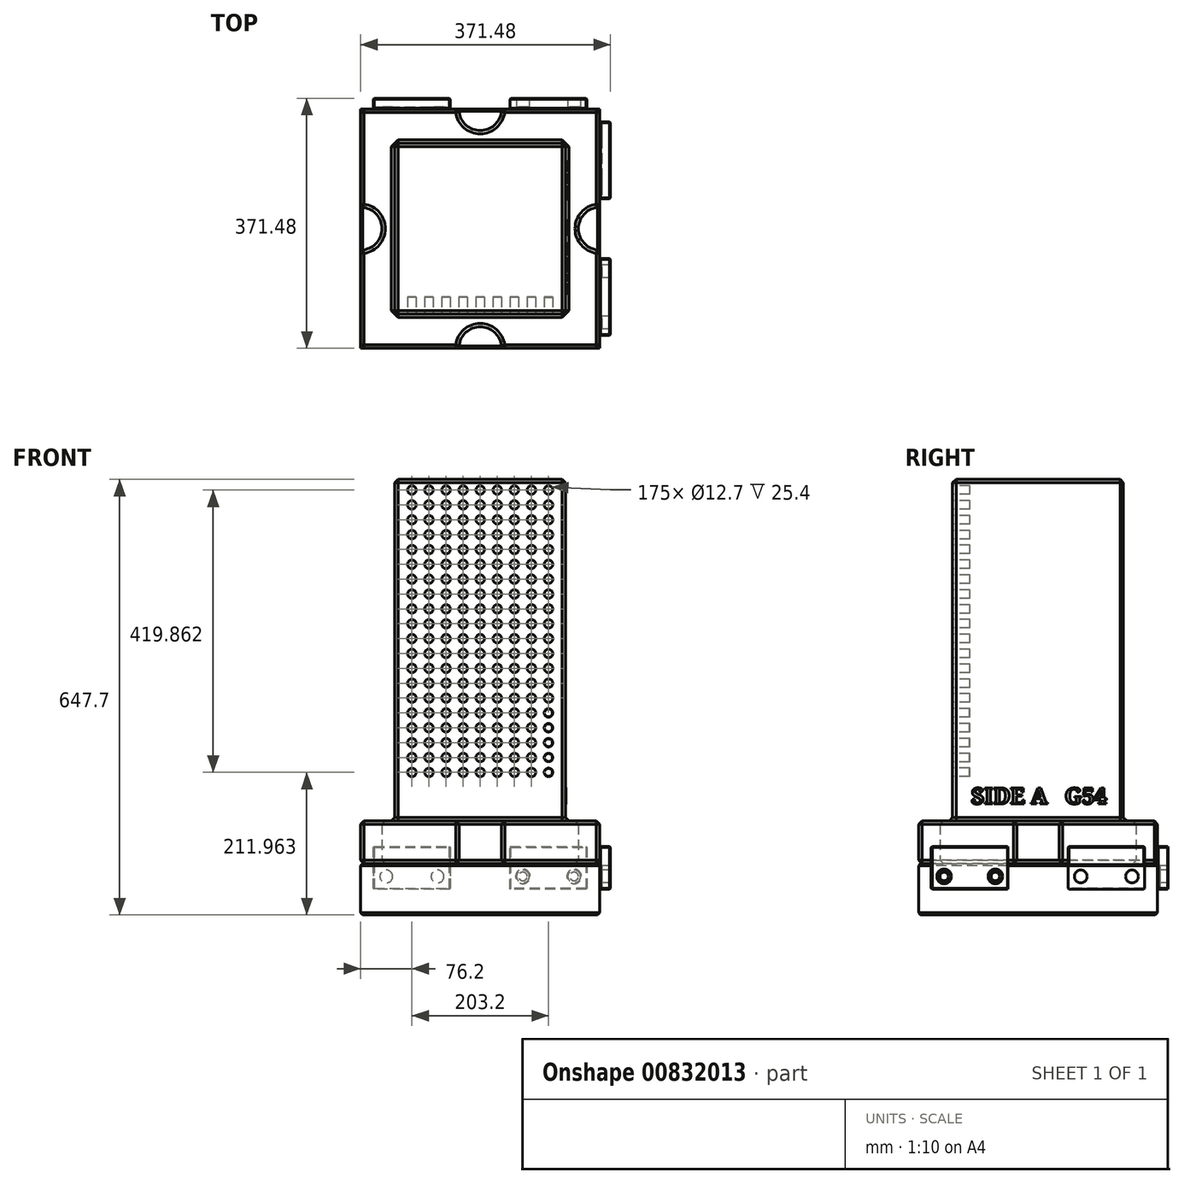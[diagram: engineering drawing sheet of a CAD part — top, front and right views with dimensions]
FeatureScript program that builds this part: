
annotation { "Feature Type Name" : "Feature", "Feature Type Description" : "" }
export const myFeature = defineFeature(function(context is Context, id is Id, definition is map)
    precondition{}
    {
        {
            var Q0;
            Q0=qCreatedBy(makeId("Top.planeOp"),FACE);
            var sketch = newSketch(context, id + "F0", { "sketchPlane" : qUnion([Q0])});
            skLineSegment(sketch, "E0.bottom", {"start": v(-127, -127) * mm, "end": v(127, -127) * mm});
            skLineSegment(sketch, "E0.top", {"start": v(-127, 127) * mm, "end": v(127, 127) * mm});
            skLineSegment(sketch, "E0.left", {"start": v(-127, -127) * mm, "end": v(-127, 127) * mm});
            skLineSegment(sketch, "E0.right", {"start": v(127, -127) * mm, "end": v(127, 127) * mm});
            skPoint(sketch, "E0.middle", {"position": v(0, 0) * mm});
            skLineSegment(sketch, "E1.bottom", {"start": v(-177.8, -177.8) * mm, "end": v(177.8, -177.8) * mm});
            skLineSegment(sketch, "E1.top", {"start": v(-177.8, 177.8) * mm, "end": v(177.8, 177.8) * mm});
            skLineSegment(sketch, "E1.left", {"start": v(-177.8, -177.8) * mm, "end": v(-177.8, 177.8) * mm});
            skLineSegment(sketch, "E1.right", {"start": v(177.8, -177.8) * mm, "end": v(177.8, 177.8) * mm});
            skSolve(sketch);
        }
        {
            var Q0;
            Q0=makeQuery(id+"F0.imprint","IMPRINT",FACE,{"disambiguationData":[TD([[makeQuery(id+"F0.imprint","IMPRINT",EDGE,{"derivedFrom":sQuery(id+"F0.wireOp",EDGE,"E0.bottom")}),1.0]])]});
            extrude(context, id + "F1", {"entities" : qUnion([Q0]), "depth" : 508 * mm});
        }
        {
            var Q0;
            Q0=makeQuery(id+"F0.imprint","IMPRINT",FACE,{"disambiguationData":[TD([[makeQuery(id+"F0.imprint","IMPRINT",EDGE,{"derivedFrom":sQuery(id+"F0.wireOp",EDGE,"E0.bottom")}),-1.0]])]});
            var Q1;
            Q1=makeQuery(id+"F0.imprint","IMPRINT",FACE,{"disambiguationData":[TD([[makeQuery(id+"F0.imprint","IMPRINT",EDGE,{"derivedFrom":sQuery(id+"F0.wireOp",EDGE,"E0.bottom")}),1.0]])]});
            extrude(context, id + "F2", {"entities" : qUnion([Q0, Q1]), "operationType" : NewBodyOperationType.ADD, "oppositeDirection" : true, "depth" : 63.5 * mm});
        }
        {
            var Q0;
            Q0=makeQuery(id+"F2.opExtrude","CAP_FACE",FACE,{"disambiguationData":[OSD([sQuery(id+"F0.wireOp",EDGE,"E1.bottom"),sQuery(id+"F0.wireOp",EDGE,"E1.top"),sQuery(id+"F0.wireOp",EDGE,"E1.left"),sQuery(id+"F0.wireOp",EDGE,"E1.right")])],"isStart":false});
            var sketch = newSketch(context, id + "F3", { "sketchPlane" : qUnion([Q0])});
            skCircle(sketch, "E2", {"center": v(-177.8, 0) * mm, "radius": 31.75 * mm});
            skCircle(sketch, "E3", {"center": v(177.8, 0) * mm, "radius": 31.75 * mm});
            skCircle(sketch, "E4", {"center": v(0, -177.8) * mm, "radius": 31.75 * mm});
            skCircle(sketch, "E5", {"center": v(0, 177.8) * mm, "radius": 31.75 * mm});
            skSolve(sketch);
        }
        {
            var Q0;
            {var subQ0=sQuery(id+"F3.wireOp",EDGE,"E5");var subQ1=makeQuery(id+"F2.opExtrude","CAP_EDGE",EDGE,{"disambiguationData":[OSD([sQuery(id+"F0.wireOp",EDGE,"E1.bottom")])],"isStart":false});var subQ2=makeQuery(id+"F3.imprint","INTERSECT",VERTEX,{"disambiguationData":[OD(0.0)],"derivedFrom":[subQ1,subQ0]});Q0=makeQuery(id+"F3.imprint","IMPRINT",FACE,{"disambiguationData":[TD([[makeQuery(id+"F3.imprint","IMPRINT",EDGE,{"disambiguationData":[TD([[subQ2,-1.0]])],"derivedFrom":subQ0}),1.0]])]});}
            var Q1;
            {var subQ0=sQuery(id+"F3.wireOp",EDGE,"E3");var subQ1=makeQuery(id+"F2.opExtrude","CAP_EDGE",EDGE,{"disambiguationData":[OSD([sQuery(id+"F0.wireOp",EDGE,"E1.right")])],"isStart":false});var subQ2=makeQuery(id+"F3.imprint","INTERSECT",VERTEX,{"disambiguationData":[OD(0.0)],"derivedFrom":[subQ1,subQ0]});Q1=makeQuery(id+"F3.imprint","IMPRINT",FACE,{"disambiguationData":[TD([[makeQuery(id+"F3.imprint","IMPRINT",EDGE,{"disambiguationData":[TD([[subQ2,-1.0]])],"derivedFrom":subQ0}),1.0]])]});}
            var Q2;
            {var subQ0=sQuery(id+"F3.wireOp",EDGE,"E2");var subQ1=makeQuery(id+"F2.opExtrude","CAP_EDGE",EDGE,{"disambiguationData":[OSD([sQuery(id+"F0.wireOp",EDGE,"E1.left")])],"isStart":false});var subQ2=makeQuery(id+"F3.imprint","INTERSECT",VERTEX,{"disambiguationData":[OD(0.0)],"derivedFrom":[subQ1,subQ0]});Q2=makeQuery(id+"F3.imprint","IMPRINT",FACE,{"disambiguationData":[TD([[makeQuery(id+"F3.imprint","IMPRINT",EDGE,{"disambiguationData":[TD([[subQ2,1.0]])],"derivedFrom":subQ0}),1.0]])]});}
            var Q3;
            {var subQ0=sQuery(id+"F3.wireOp",EDGE,"E4");var subQ1=makeQuery(id+"F2.opExtrude","CAP_EDGE",EDGE,{"disambiguationData":[OSD([sQuery(id+"F0.wireOp",EDGE,"E1.top")])],"isStart":false});var subQ2=makeQuery(id+"F3.imprint","INTERSECT",VERTEX,{"disambiguationData":[OD(0.0)],"derivedFrom":[subQ1,subQ0]});Q3=makeQuery(id+"F3.imprint","IMPRINT",FACE,{"disambiguationData":[TD([[makeQuery(id+"F3.imprint","IMPRINT",EDGE,{"disambiguationData":[TD([[subQ2,1.0]])],"derivedFrom":subQ0}),1.0]])]});}
            var Q4;
            Q4=makeQuery(id+"F2.opExtrude","CAP_FACE",FACE,{"disambiguationData":[OSD([sQuery(id+"F0.wireOp",EDGE,"E1.bottom"),sQuery(id+"F0.wireOp",EDGE,"E1.top"),sQuery(id+"F0.wireOp",EDGE,"E1.left"),sQuery(id+"F0.wireOp",EDGE,"E1.right")])],"isStart":true});
            extrude(context, id + "F4", {"entities" : qUnion([Q0, Q1, Q2, Q3]), "operationType" : NewBodyOperationType.REMOVE, "endBound" : BoundingType.UP_TO_SURFACE, "oppositeDirection" : true, "endBoundEntityFace" : qUnion([Q4]), "depth" : 25.4 * mm});
        }
        {
            var Q0;
            Q0=makeQuery(id+"F1.opExtrude","CAP_FACE",FACE,{"disambiguationData":[OSD([sQuery(id+"F0.wireOp",EDGE,"E0.bottom"),sQuery(id+"F0.wireOp",EDGE,"E0.top"),sQuery(id+"F0.wireOp",EDGE,"E0.left"),sQuery(id+"F0.wireOp",EDGE,"E0.right")])],"isStart":false});
            var Q1;
            Q1=makeQuery(id+"F1.opExtrude","SWEPT_FACE",FACE,{"disambiguationData":[OSD([sQuery(id+"F0.wireOp",EDGE,"E0.right")])]});
            var Q2;
            Q2=makeQuery(id+"F1.opExtrude","SWEPT_FACE",FACE,{"disambiguationData":[OSD([sQuery(id+"F0.wireOp",EDGE,"E0.top")])]});
            var Q3;
            Q3=makeQuery(id+"F1.opExtrude","SWEPT_FACE",FACE,{"disambiguationData":[OSD([sQuery(id+"F0.wireOp",EDGE,"E0.left")])]});
            var Q4;
            Q4=makeQuery(id+"F1.opExtrude","SWEPT_FACE",FACE,{"disambiguationData":[OSD([sQuery(id+"F0.wireOp",EDGE,"E0.bottom")])]});
            var Q5;
            {var subQ1=sQuery(id+"F0.wireOp",EDGE,"E1.left");var subQ3=sQuery(id+"F0.wireOp",EDGE,"E1.bottom");Q5=makeQuery(id+"F4.boolean.opBoolean","SPLIT",FACE,{"disambiguationData":[TD([makeQuery(id+"F2.opExtrude","SWEPT_FACE",FACE,{"disambiguationData":[OSD([subQ1])]})])],"derivedFrom":makeQuery(id+"F2.opExtrude","SWEPT_FACE",FACE,{"disambiguationData":[OSD([subQ3])]})});}
            var Q6;
            {var subQ0=sQuery(id+"F0.wireOp",EDGE,"E1.right");var subQ3=sQuery(id+"F0.wireOp",EDGE,"E1.bottom");Q6=makeQuery(id+"F4.boolean.opBoolean","SPLIT",FACE,{"disambiguationData":[TD([makeQuery(id+"F2.opExtrude","SWEPT_FACE",FACE,{"disambiguationData":[OSD([subQ0])]})])],"derivedFrom":makeQuery(id+"F2.opExtrude","SWEPT_FACE",FACE,{"disambiguationData":[OSD([subQ3])]})});}
            var Q7;
            Q7=makeQuery(id+"F4.boolean.opBoolean","COPY",FACE,{"derivedFrom":makeQuery(id+"F4.opExtrude","SWEPT_FACE",FACE,{"disambiguationData":[OSD([sQuery(id+"F3.wireOp",EDGE,"E5")])]})});
            var Q8;
            Q8=makeQuery(id+"F4.boolean.opBoolean","COPY",FACE,{"derivedFrom":makeQuery(id+"F4.opExtrude","SWEPT_FACE",FACE,{"disambiguationData":[OSD([sQuery(id+"F3.wireOp",EDGE,"E3")])]})});
            var Q9;
            {var subQ0=sQuery(id+"F0.wireOp",EDGE,"E1.bottom");var subQ1=sQuery(id+"F0.wireOp",EDGE,"E1.right");Q9=makeQuery(id+"F4.boolean.opBoolean","SPLIT",FACE,{"disambiguationData":[TD([makeQuery(id+"F2.opExtrude","SWEPT_FACE",FACE,{"disambiguationData":[OSD([subQ0])]})])],"derivedFrom":makeQuery(id+"F2.opExtrude","SWEPT_FACE",FACE,{"disambiguationData":[OSD([subQ1])]})});}
            var Q10;
            {var subQ0=sQuery(id+"F0.wireOp",EDGE,"E1.right");var subQ2=sQuery(id+"F0.wireOp",EDGE,"E1.top");Q10=makeQuery(id+"F4.boolean.opBoolean","SPLIT",FACE,{"disambiguationData":[TD([makeQuery(id+"F2.opExtrude","SWEPT_FACE",FACE,{"disambiguationData":[OSD([subQ2])]})])],"derivedFrom":makeQuery(id+"F2.opExtrude","SWEPT_FACE",FACE,{"disambiguationData":[OSD([subQ0])]})});}
            var Q11;
            {var subQ0=sQuery(id+"F0.wireOp",EDGE,"E1.right");var subQ2=sQuery(id+"F0.wireOp",EDGE,"E1.top");Q11=makeQuery(id+"F4.boolean.opBoolean","SPLIT",FACE,{"disambiguationData":[TD([makeQuery(id+"F2.opExtrude","SWEPT_FACE",FACE,{"disambiguationData":[OSD([subQ0])]})])],"derivedFrom":makeQuery(id+"F2.opExtrude","SWEPT_FACE",FACE,{"disambiguationData":[OSD([subQ2])]})});}
            var Q12;
            Q12=makeQuery(id+"F4.boolean.opBoolean","COPY",FACE,{"derivedFrom":makeQuery(id+"F4.opExtrude","SWEPT_FACE",FACE,{"disambiguationData":[OSD([sQuery(id+"F3.wireOp",EDGE,"E4")])]})});
            var Q13;
            {var subQ1=sQuery(id+"F0.wireOp",EDGE,"E1.left");var subQ2=sQuery(id+"F0.wireOp",EDGE,"E1.top");Q13=makeQuery(id+"F4.boolean.opBoolean","SPLIT",FACE,{"disambiguationData":[TD([makeQuery(id+"F2.opExtrude","SWEPT_FACE",FACE,{"disambiguationData":[OSD([subQ1])]})])],"derivedFrom":makeQuery(id+"F2.opExtrude","SWEPT_FACE",FACE,{"disambiguationData":[OSD([subQ2])]})});}
            var Q14;
            {var subQ1=sQuery(id+"F0.wireOp",EDGE,"E1.left");var subQ2=sQuery(id+"F0.wireOp",EDGE,"E1.top");Q14=makeQuery(id+"F4.boolean.opBoolean","SPLIT",FACE,{"disambiguationData":[TD([makeQuery(id+"F2.opExtrude","SWEPT_FACE",FACE,{"disambiguationData":[OSD([subQ2])]})])],"derivedFrom":makeQuery(id+"F2.opExtrude","SWEPT_FACE",FACE,{"disambiguationData":[OSD([subQ1])]})});}
            var Q15;
            Q15=makeQuery(id+"F4.boolean.opBoolean","COPY",FACE,{"derivedFrom":makeQuery(id+"F4.opExtrude","SWEPT_FACE",FACE,{"disambiguationData":[OSD([sQuery(id+"F3.wireOp",EDGE,"E2")])]})});
            var Q16;
            {var subQ0=sQuery(id+"F0.wireOp",EDGE,"E1.bottom");var subQ2=sQuery(id+"F0.wireOp",EDGE,"E1.left");Q16=makeQuery(id+"F4.boolean.opBoolean","SPLIT",FACE,{"disambiguationData":[TD([makeQuery(id+"F2.opExtrude","SWEPT_FACE",FACE,{"disambiguationData":[OSD([subQ0])]})])],"derivedFrom":makeQuery(id+"F2.opExtrude","SWEPT_FACE",FACE,{"disambiguationData":[OSD([subQ2])]})});}
            chamfer(context, id + "F5", {"entities" : qUnion([Q0, Q1, Q2, Q3, Q4, Q5, Q6, Q7, Q8, Q9, Q10, Q11, Q12, Q13, Q14, Q15, Q16]), "width" : 5.08 * mm, "tangentPropagation" : true});
        }
        {
            var Q0;
            Q0=makeQuery(id+"F1.opExtrude","SWEPT_FACE",FACE,{"disambiguationData":[OSD([sQuery(id+"F0.wireOp",EDGE,"E0.bottom")])]});
            var sketch = newSketch(context, id + "F6", { "sketchPlane" : qUnion([Q0])});
            skCircle(sketch, "E6", {"center": v(-101.6, 492.13) * mm, "radius": 6.35 * mm});
            skLineSegment(sketch, "E7", {"start": v(0, 0) * mm, "end": v(0, 678.57) * mm, "construction": true});
            skCircle(sketch, "E8.0.1.0", {"center": v(-101.6, 470.03) * mm, "radius": 6.35 * mm});
            skCircle(sketch, "E8.0.2.0", {"center": v(-101.6, 447.93) * mm, "radius": 6.35 * mm});
            skCircle(sketch, "E8.0.3.0", {"center": v(-101.6, 425.83) * mm, "radius": 6.35 * mm});
            skCircle(sketch, "E8.0.4.0", {"center": v(-101.6, 403.73) * mm, "radius": 6.35 * mm});
            skCircle(sketch, "E8.0.5.0", {"center": v(-101.6, 381.63) * mm, "radius": 6.35 * mm});
            skCircle(sketch, "E8.0.6.0", {"center": v(-101.6, 359.54) * mm, "radius": 6.35 * mm});
            skCircle(sketch, "E8.0.7.0", {"center": v(-101.6, 337.44) * mm, "radius": 6.35 * mm});
            skCircle(sketch, "E8.0.8.0", {"center": v(-101.6, 315.34) * mm, "radius": 6.35 * mm});
            skCircle(sketch, "E8.0.9.0", {"center": v(-101.6, 293.24) * mm, "radius": 6.35 * mm});
            skCircle(sketch, "E8.0.10.0", {"center": v(-101.6, 271.14) * mm, "radius": 6.35 * mm});
            skCircle(sketch, "E8.0.11.0", {"center": v(-101.6, 249.05) * mm, "radius": 6.35 * mm});
            skCircle(sketch, "E8.0.12.0", {"center": v(-101.6, 226.95) * mm, "radius": 6.35 * mm});
            skCircle(sketch, "E8.0.13.0", {"center": v(-101.6, 204.85) * mm, "radius": 6.35 * mm});
            skCircle(sketch, "E8.0.14.0", {"center": v(-101.6, 182.75) * mm, "radius": 6.35 * mm});
            skCircle(sketch, "E8.1.0.0", {"center": v(-76.2, 492.13) * mm, "radius": 6.35 * mm});
            skCircle(sketch, "E8.1.1.0", {"center": v(-76.2, 470.03) * mm, "radius": 6.35 * mm});
            skCircle(sketch, "E8.1.2.0", {"center": v(-76.2, 447.93) * mm, "radius": 6.35 * mm});
            skCircle(sketch, "E8.1.3.0", {"center": v(-76.2, 425.83) * mm, "radius": 6.35 * mm});
            skCircle(sketch, "E8.1.4.0", {"center": v(-76.2, 403.73) * mm, "radius": 6.35 * mm});
            skCircle(sketch, "E8.1.5.0", {"center": v(-76.2, 381.63) * mm, "radius": 6.35 * mm});
            skCircle(sketch, "E8.1.6.0", {"center": v(-76.2, 359.54) * mm, "radius": 6.35 * mm});
            skCircle(sketch, "E8.1.7.0", {"center": v(-76.2, 337.44) * mm, "radius": 6.35 * mm});
            skCircle(sketch, "E8.1.8.0", {"center": v(-76.2, 315.34) * mm, "radius": 6.35 * mm});
            skCircle(sketch, "E8.1.9.0", {"center": v(-76.2, 293.24) * mm, "radius": 6.35 * mm});
            skCircle(sketch, "E8.1.10.0", {"center": v(-76.2, 271.14) * mm, "radius": 6.35 * mm});
            skCircle(sketch, "E8.1.11.0", {"center": v(-76.2, 249.05) * mm, "radius": 6.35 * mm});
            skCircle(sketch, "E8.1.12.0", {"center": v(-76.2, 226.95) * mm, "radius": 6.35 * mm});
            skCircle(sketch, "E8.1.13.0", {"center": v(-76.2, 204.85) * mm, "radius": 6.35 * mm});
            skCircle(sketch, "E8.1.14.0", {"center": v(-76.2, 182.75) * mm, "radius": 6.35 * mm});
            skCircle(sketch, "E8.2.0.0", {"center": v(-50.8, 492.13) * mm, "radius": 6.35 * mm});
            skCircle(sketch, "E8.2.1.0", {"center": v(-50.8, 470.03) * mm, "radius": 6.35 * mm});
            skCircle(sketch, "E8.2.2.0", {"center": v(-50.8, 447.93) * mm, "radius": 6.35 * mm});
            skCircle(sketch, "E8.2.3.0", {"center": v(-50.8, 425.83) * mm, "radius": 6.35 * mm});
            skCircle(sketch, "E8.2.4.0", {"center": v(-50.8, 403.73) * mm, "radius": 6.35 * mm});
            skCircle(sketch, "E8.2.5.0", {"center": v(-50.8, 381.63) * mm, "radius": 6.35 * mm});
            skCircle(sketch, "E8.2.6.0", {"center": v(-50.8, 359.54) * mm, "radius": 6.35 * mm});
            skCircle(sketch, "E8.2.7.0", {"center": v(-50.8, 337.44) * mm, "radius": 6.35 * mm});
            skCircle(sketch, "E8.2.8.0", {"center": v(-50.8, 315.34) * mm, "radius": 6.35 * mm});
            skCircle(sketch, "E8.2.9.0", {"center": v(-50.8, 293.24) * mm, "radius": 6.35 * mm});
            skCircle(sketch, "E8.2.10.0", {"center": v(-50.8, 271.14) * mm, "radius": 6.35 * mm});
            skCircle(sketch, "E8.2.11.0", {"center": v(-50.8, 249.05) * mm, "radius": 6.35 * mm});
            skCircle(sketch, "E8.2.12.0", {"center": v(-50.8, 226.95) * mm, "radius": 6.35 * mm});
            skCircle(sketch, "E8.2.13.0", {"center": v(-50.8, 204.85) * mm, "radius": 6.35 * mm});
            skCircle(sketch, "E8.2.14.0", {"center": v(-50.8, 182.75) * mm, "radius": 6.35 * mm});
            skCircle(sketch, "E8.3.0.0", {"center": v(-25.4, 492.13) * mm, "radius": 6.35 * mm});
            skCircle(sketch, "E8.3.1.0", {"center": v(-25.4, 470.03) * mm, "radius": 6.35 * mm});
            skCircle(sketch, "E8.3.2.0", {"center": v(-25.4, 447.93) * mm, "radius": 6.35 * mm});
            skCircle(sketch, "E8.3.3.0", {"center": v(-25.4, 425.83) * mm, "radius": 6.35 * mm});
            skCircle(sketch, "E8.3.4.0", {"center": v(-25.4, 403.73) * mm, "radius": 6.35 * mm});
            skCircle(sketch, "E8.3.5.0", {"center": v(-25.4, 381.63) * mm, "radius": 6.35 * mm});
            skCircle(sketch, "E8.3.6.0", {"center": v(-25.4, 359.54) * mm, "radius": 6.35 * mm});
            skCircle(sketch, "E8.3.7.0", {"center": v(-25.4, 337.44) * mm, "radius": 6.35 * mm});
            skCircle(sketch, "E8.3.8.0", {"center": v(-25.4, 315.34) * mm, "radius": 6.35 * mm});
            skCircle(sketch, "E8.3.9.0", {"center": v(-25.4, 293.24) * mm, "radius": 6.35 * mm});
            skCircle(sketch, "E8.3.10.0", {"center": v(-25.4, 271.14) * mm, "radius": 6.35 * mm});
            skCircle(sketch, "E8.3.11.0", {"center": v(-25.4, 249.05) * mm, "radius": 6.35 * mm});
            skCircle(sketch, "E8.3.12.0", {"center": v(-25.4, 226.95) * mm, "radius": 6.35 * mm});
            skCircle(sketch, "E8.3.13.0", {"center": v(-25.4, 204.85) * mm, "radius": 6.35 * mm});
            skCircle(sketch, "E8.3.14.0", {"center": v(-25.4, 182.75) * mm, "radius": 6.35 * mm});
            skCircle(sketch, "E8.4.0.0", {"center": v(0, 492.13) * mm, "radius": 6.35 * mm});
            skCircle(sketch, "E8.4.1.0", {"center": v(0, 470.03) * mm, "radius": 6.35 * mm});
            skCircle(sketch, "E8.4.2.0", {"center": v(0, 447.93) * mm, "radius": 6.35 * mm});
            skCircle(sketch, "E8.4.3.0", {"center": v(0, 425.83) * mm, "radius": 6.35 * mm});
            skCircle(sketch, "E8.4.4.0", {"center": v(0, 403.73) * mm, "radius": 6.35 * mm});
            skCircle(sketch, "E8.4.5.0", {"center": v(0, 381.63) * mm, "radius": 6.35 * mm});
            skCircle(sketch, "E8.4.6.0", {"center": v(0, 359.54) * mm, "radius": 6.35 * mm});
            skCircle(sketch, "E8.4.7.0", {"center": v(0, 337.44) * mm, "radius": 6.35 * mm});
            skCircle(sketch, "E8.4.8.0", {"center": v(0, 315.34) * mm, "radius": 6.35 * mm});
            skCircle(sketch, "E8.4.9.0", {"center": v(0, 293.24) * mm, "radius": 6.35 * mm});
            skCircle(sketch, "E8.4.10.0", {"center": v(0, 271.14) * mm, "radius": 6.35 * mm});
            skCircle(sketch, "E8.4.11.0", {"center": v(0, 249.05) * mm, "radius": 6.35 * mm});
            skCircle(sketch, "E8.4.12.0", {"center": v(0, 226.95) * mm, "radius": 6.35 * mm});
            skCircle(sketch, "E8.4.13.0", {"center": v(0, 204.85) * mm, "radius": 6.35 * mm});
            skCircle(sketch, "E8.4.14.0", {"center": v(0, 182.75) * mm, "radius": 6.35 * mm});
            skCircle(sketch, "E8.5.0.0", {"center": v(25.4, 492.13) * mm, "radius": 6.35 * mm});
            skCircle(sketch, "E8.5.1.0", {"center": v(25.4, 470.03) * mm, "radius": 6.35 * mm});
            skCircle(sketch, "E8.5.2.0", {"center": v(25.4, 447.93) * mm, "radius": 6.35 * mm});
            skCircle(sketch, "E8.5.3.0", {"center": v(25.4, 425.83) * mm, "radius": 6.35 * mm});
            skCircle(sketch, "E8.5.4.0", {"center": v(25.4, 403.73) * mm, "radius": 6.35 * mm});
            skCircle(sketch, "E8.5.5.0", {"center": v(25.4, 381.63) * mm, "radius": 6.35 * mm});
            skCircle(sketch, "E8.5.6.0", {"center": v(25.4, 359.54) * mm, "radius": 6.35 * mm});
            skCircle(sketch, "E8.5.7.0", {"center": v(25.4, 337.44) * mm, "radius": 6.35 * mm});
            skCircle(sketch, "E8.5.8.0", {"center": v(25.4, 315.34) * mm, "radius": 6.35 * mm});
            skCircle(sketch, "E8.5.9.0", {"center": v(25.4, 293.24) * mm, "radius": 6.35 * mm});
            skCircle(sketch, "E8.5.10.0", {"center": v(25.4, 271.14) * mm, "radius": 6.35 * mm});
            skCircle(sketch, "E8.5.11.0", {"center": v(25.4, 249.05) * mm, "radius": 6.35 * mm});
            skCircle(sketch, "E8.5.12.0", {"center": v(25.4, 226.95) * mm, "radius": 6.35 * mm});
            skCircle(sketch, "E8.5.13.0", {"center": v(25.4, 204.85) * mm, "radius": 6.35 * mm});
            skCircle(sketch, "E8.5.14.0", {"center": v(25.4, 182.75) * mm, "radius": 6.35 * mm});
            skCircle(sketch, "E8.6.0.0", {"center": v(50.8, 492.13) * mm, "radius": 6.35 * mm});
            skCircle(sketch, "E8.6.1.0", {"center": v(50.8, 470.03) * mm, "radius": 6.35 * mm});
            skCircle(sketch, "E8.6.2.0", {"center": v(50.8, 447.93) * mm, "radius": 6.35 * mm});
            skCircle(sketch, "E8.6.3.0", {"center": v(50.8, 425.83) * mm, "radius": 6.35 * mm});
            skCircle(sketch, "E8.6.4.0", {"center": v(50.8, 403.73) * mm, "radius": 6.35 * mm});
            skCircle(sketch, "E8.6.5.0", {"center": v(50.8, 381.63) * mm, "radius": 6.35 * mm});
            skCircle(sketch, "E8.6.6.0", {"center": v(50.8, 359.54) * mm, "radius": 6.35 * mm});
            skCircle(sketch, "E8.6.7.0", {"center": v(50.8, 337.44) * mm, "radius": 6.35 * mm});
            skCircle(sketch, "E8.6.8.0", {"center": v(50.8, 315.34) * mm, "radius": 6.35 * mm});
            skCircle(sketch, "E8.6.9.0", {"center": v(50.8, 293.24) * mm, "radius": 6.35 * mm});
            skCircle(sketch, "E8.6.10.0", {"center": v(50.8, 271.14) * mm, "radius": 6.35 * mm});
            skCircle(sketch, "E8.6.11.0", {"center": v(50.8, 249.05) * mm, "radius": 6.35 * mm});
            skCircle(sketch, "E8.6.12.0", {"center": v(50.8, 226.95) * mm, "radius": 6.35 * mm});
            skCircle(sketch, "E8.6.13.0", {"center": v(50.8, 204.85) * mm, "radius": 6.35 * mm});
            skCircle(sketch, "E8.6.14.0", {"center": v(50.8, 182.75) * mm, "radius": 6.35 * mm});
            skCircle(sketch, "E8.7.0.0", {"center": v(76.2, 492.13) * mm, "radius": 6.35 * mm});
            skCircle(sketch, "E8.7.1.0", {"center": v(76.2, 470.03) * mm, "radius": 6.35 * mm});
            skCircle(sketch, "E8.7.2.0", {"center": v(76.2, 447.93) * mm, "radius": 6.35 * mm});
            skCircle(sketch, "E8.7.3.0", {"center": v(76.2, 425.83) * mm, "radius": 6.35 * mm});
            skCircle(sketch, "E8.7.4.0", {"center": v(76.2, 403.73) * mm, "radius": 6.35 * mm});
            skCircle(sketch, "E8.7.5.0", {"center": v(76.2, 381.63) * mm, "radius": 6.35 * mm});
            skCircle(sketch, "E8.7.6.0", {"center": v(76.2, 359.54) * mm, "radius": 6.35 * mm});
            skCircle(sketch, "E8.7.7.0", {"center": v(76.2, 337.44) * mm, "radius": 6.35 * mm});
            skCircle(sketch, "E8.7.8.0", {"center": v(76.2, 315.34) * mm, "radius": 6.35 * mm});
            skCircle(sketch, "E8.7.9.0", {"center": v(76.2, 293.24) * mm, "radius": 6.35 * mm});
            skCircle(sketch, "E8.7.10.0", {"center": v(76.2, 271.14) * mm, "radius": 6.35 * mm});
            skCircle(sketch, "E8.7.11.0", {"center": v(76.2, 249.05) * mm, "radius": 6.35 * mm});
            skCircle(sketch, "E8.7.12.0", {"center": v(76.2, 226.95) * mm, "radius": 6.35 * mm});
            skCircle(sketch, "E8.7.13.0", {"center": v(76.2, 204.85) * mm, "radius": 6.35 * mm});
            skCircle(sketch, "E8.7.14.0", {"center": v(76.2, 182.75) * mm, "radius": 6.35 * mm});
            skCircle(sketch, "E8.8.0.0", {"center": v(101.6, 492.13) * mm, "radius": 6.35 * mm});
            skCircle(sketch, "E8.8.1.0", {"center": v(101.6, 470.03) * mm, "radius": 6.35 * mm});
            skCircle(sketch, "E8.8.2.0", {"center": v(101.6, 447.93) * mm, "radius": 6.35 * mm});
            skCircle(sketch, "E8.8.3.0", {"center": v(101.6, 425.83) * mm, "radius": 6.35 * mm});
            skCircle(sketch, "E8.8.4.0", {"center": v(101.6, 403.73) * mm, "radius": 6.35 * mm});
            skCircle(sketch, "E8.8.5.0", {"center": v(101.6, 381.63) * mm, "radius": 6.35 * mm});
            skCircle(sketch, "E8.8.6.0", {"center": v(101.6, 359.54) * mm, "radius": 6.35 * mm});
            skCircle(sketch, "E8.8.7.0", {"center": v(101.6, 337.44) * mm, "radius": 6.35 * mm});
            skCircle(sketch, "E8.8.8.0", {"center": v(101.6, 315.34) * mm, "radius": 6.35 * mm});
            skCircle(sketch, "E8.8.9.0", {"center": v(101.6, 293.24) * mm, "radius": 6.35 * mm});
            skCircle(sketch, "E8.8.10.0", {"center": v(101.6, 271.14) * mm, "radius": 6.35 * mm});
            skCircle(sketch, "E8.8.11.0", {"center": v(101.6, 249.05) * mm, "radius": 6.35 * mm});
            skCircle(sketch, "E8.8.12.0", {"center": v(101.6, 226.95) * mm, "radius": 6.35 * mm});
            skCircle(sketch, "E8.8.13.0", {"center": v(101.6, 204.85) * mm, "radius": 6.35 * mm});
            skCircle(sketch, "E8.8.14.0", {"center": v(101.6, 182.75) * mm, "radius": 6.35 * mm});
            skLineSegment(sketch, "E8.direction1", {"start": v(-101.6, 492.13) * mm, "end": v(-76.2, 492.13) * mm, "construction": true});
            skLineSegment(sketch, "E8.direction2", {"start": v(-101.6, 492.13) * mm, "end": v(-101.6, 470.03) * mm, "construction": true});
            skCircle(sketch, "E9.0.0.15", {"center": v(-101.6, 160.65) * mm, "radius": 6.35 * mm});
            skCircle(sketch, "E9.0.0.16", {"center": v(-101.6, 138.56) * mm, "radius": 6.35 * mm});
            skCircle(sketch, "E9.0.0.17", {"center": v(-101.6, 116.46) * mm, "radius": 6.35 * mm});
            skCircle(sketch, "E9.0.0.18", {"center": v(-101.6, 94.36) * mm, "radius": 6.35 * mm});
            skCircle(sketch, "E9.0.0.19", {"center": v(-101.6, 72.26) * mm, "radius": 6.35 * mm});
            skCircle(sketch, "E9.0.1.15", {"center": v(-76.2, 160.65) * mm, "radius": 6.35 * mm});
            skCircle(sketch, "E9.0.1.16", {"center": v(-76.2, 138.56) * mm, "radius": 6.35 * mm});
            skCircle(sketch, "E9.0.1.17", {"center": v(-76.2, 116.46) * mm, "radius": 6.35 * mm});
            skCircle(sketch, "E9.0.1.18", {"center": v(-76.2, 94.36) * mm, "radius": 6.35 * mm});
            skCircle(sketch, "E9.0.1.19", {"center": v(-76.2, 72.26) * mm, "radius": 6.35 * mm});
            skCircle(sketch, "E9.0.2.15", {"center": v(-50.8, 160.65) * mm, "radius": 6.35 * mm});
            skCircle(sketch, "E9.0.2.16", {"center": v(-50.8, 138.56) * mm, "radius": 6.35 * mm});
            skCircle(sketch, "E9.0.2.17", {"center": v(-50.8, 116.46) * mm, "radius": 6.35 * mm});
            skCircle(sketch, "E9.0.2.18", {"center": v(-50.8, 94.36) * mm, "radius": 6.35 * mm});
            skCircle(sketch, "E9.0.2.19", {"center": v(-50.8, 72.26) * mm, "radius": 6.35 * mm});
            skCircle(sketch, "E9.0.3.15", {"center": v(-25.4, 160.65) * mm, "radius": 6.35 * mm});
            skCircle(sketch, "E9.0.3.16", {"center": v(-25.4, 138.56) * mm, "radius": 6.35 * mm});
            skCircle(sketch, "E9.0.3.17", {"center": v(-25.4, 116.46) * mm, "radius": 6.35 * mm});
            skCircle(sketch, "E9.0.3.18", {"center": v(-25.4, 94.36) * mm, "radius": 6.35 * mm});
            skCircle(sketch, "E9.0.3.19", {"center": v(-25.4, 72.26) * mm, "radius": 6.35 * mm});
            skCircle(sketch, "E9.0.4.15", {"center": v(0, 160.65) * mm, "radius": 6.35 * mm});
            skCircle(sketch, "E9.0.4.16", {"center": v(0, 138.56) * mm, "radius": 6.35 * mm});
            skCircle(sketch, "E9.0.4.17", {"center": v(0, 116.46) * mm, "radius": 6.35 * mm});
            skCircle(sketch, "E9.0.4.18", {"center": v(0, 94.36) * mm, "radius": 6.35 * mm});
            skCircle(sketch, "E9.0.4.19", {"center": v(0, 72.26) * mm, "radius": 6.35 * mm});
            skCircle(sketch, "E9.0.5.15", {"center": v(25.4, 160.65) * mm, "radius": 6.35 * mm});
            skCircle(sketch, "E9.0.5.16", {"center": v(25.4, 138.56) * mm, "radius": 6.35 * mm});
            skCircle(sketch, "E9.0.5.17", {"center": v(25.4, 116.46) * mm, "radius": 6.35 * mm});
            skCircle(sketch, "E9.0.5.18", {"center": v(25.4, 94.36) * mm, "radius": 6.35 * mm});
            skCircle(sketch, "E9.0.5.19", {"center": v(25.4, 72.26) * mm, "radius": 6.35 * mm});
            skCircle(sketch, "E9.0.6.15", {"center": v(50.8, 160.65) * mm, "radius": 6.35 * mm});
            skCircle(sketch, "E9.0.6.16", {"center": v(50.8, 138.56) * mm, "radius": 6.35 * mm});
            skCircle(sketch, "E9.0.6.17", {"center": v(50.8, 116.46) * mm, "radius": 6.35 * mm});
            skCircle(sketch, "E9.0.6.18", {"center": v(50.8, 94.36) * mm, "radius": 6.35 * mm});
            skCircle(sketch, "E9.0.6.19", {"center": v(50.8, 72.26) * mm, "radius": 6.35 * mm});
            skCircle(sketch, "E9.0.7.15", {"center": v(76.2, 160.65) * mm, "radius": 6.35 * mm});
            skCircle(sketch, "E9.0.7.16", {"center": v(76.2, 138.56) * mm, "radius": 6.35 * mm});
            skCircle(sketch, "E9.0.7.17", {"center": v(76.2, 116.46) * mm, "radius": 6.35 * mm});
            skCircle(sketch, "E9.0.7.18", {"center": v(76.2, 94.36) * mm, "radius": 6.35 * mm});
            skCircle(sketch, "E9.0.7.19", {"center": v(76.2, 72.26) * mm, "radius": 6.35 * mm});
            skCircle(sketch, "E9.0.8.15", {"center": v(101.6, 160.65) * mm, "radius": 6.35 * mm});
            skCircle(sketch, "E9.0.8.16", {"center": v(101.6, 138.56) * mm, "radius": 6.35 * mm});
            skCircle(sketch, "E9.0.8.17", {"center": v(101.6, 116.46) * mm, "radius": 6.35 * mm});
            skCircle(sketch, "E9.0.8.18", {"center": v(101.6, 94.36) * mm, "radius": 6.35 * mm});
            skCircle(sketch, "E9.0.8.19", {"center": v(101.6, 72.26) * mm, "radius": 6.35 * mm});
            skSolve(sketch);
        }
        {
            var Q0;
            Q0=qSketchRegion(id+"F6",true);
            extrude(context, id + "F7", {"entities" : qUnion([Q0]), "operationType" : NewBodyOperationType.REMOVE, "oppositeDirection" : true, "depth" : 25.4 * mm});
        }
        {
            var Q0;
            Q0=makeQuery(id+"F7.boolean.opBoolean","COPY",EDGE,{"derivedFrom":makeQuery(id+"F7.opExtrude","CAP_EDGE",EDGE,{"disambiguationData":[OSD([sQuery(id+"F6.wireOp",EDGE,"E6")])],"isStart":true})});
            var Q1;
            Q1=makeQuery(id+"F7.boolean.opBoolean","COPY",EDGE,{"derivedFrom":makeQuery(id+"F7.opExtrude","CAP_EDGE",EDGE,{"disambiguationData":[OSD([sQuery(id+"F6.wireOp",EDGE,"E8.0.1.0")])],"isStart":true})});
            var Q2;
            Q2=makeQuery(id+"F7.boolean.opBoolean","COPY",EDGE,{"derivedFrom":makeQuery(id+"F7.opExtrude","CAP_EDGE",EDGE,{"disambiguationData":[OSD([sQuery(id+"F6.wireOp",EDGE,"E8.0.2.0")])],"isStart":true})});
            var Q3;
            Q3=makeQuery(id+"F7.boolean.opBoolean","COPY",EDGE,{"derivedFrom":makeQuery(id+"F7.opExtrude","CAP_EDGE",EDGE,{"disambiguationData":[OSD([sQuery(id+"F6.wireOp",EDGE,"E8.0.3.0")])],"isStart":true})});
            var Q4;
            Q4=makeQuery(id+"F7.boolean.opBoolean","COPY",EDGE,{"derivedFrom":makeQuery(id+"F7.opExtrude","CAP_EDGE",EDGE,{"disambiguationData":[OSD([sQuery(id+"F6.wireOp",EDGE,"E8.0.4.0")])],"isStart":true})});
            var Q5;
            Q5=makeQuery(id+"F7.boolean.opBoolean","COPY",EDGE,{"derivedFrom":makeQuery(id+"F7.opExtrude","CAP_EDGE",EDGE,{"disambiguationData":[OSD([sQuery(id+"F6.wireOp",EDGE,"E8.0.6.0")])],"isStart":true})});
            var Q6;
            Q6=makeQuery(id+"F7.boolean.opBoolean","COPY",EDGE,{"derivedFrom":makeQuery(id+"F7.opExtrude","CAP_EDGE",EDGE,{"disambiguationData":[OSD([sQuery(id+"F6.wireOp",EDGE,"E8.0.5.0")])],"isStart":true})});
            var Q7;
            Q7=makeQuery(id+"F7.boolean.opBoolean","COPY",EDGE,{"derivedFrom":makeQuery(id+"F7.opExtrude","CAP_EDGE",EDGE,{"disambiguationData":[OSD([sQuery(id+"F6.wireOp",EDGE,"E8.0.7.0")])],"isStart":true})});
            var Q8;
            Q8=makeQuery(id+"F7.boolean.opBoolean","COPY",EDGE,{"derivedFrom":makeQuery(id+"F7.opExtrude","CAP_EDGE",EDGE,{"disambiguationData":[OSD([sQuery(id+"F6.wireOp",EDGE,"E8.0.8.0")])],"isStart":true})});
            var Q9;
            Q9=makeQuery(id+"F7.boolean.opBoolean","COPY",EDGE,{"derivedFrom":makeQuery(id+"F7.opExtrude","CAP_EDGE",EDGE,{"disambiguationData":[OSD([sQuery(id+"F6.wireOp",EDGE,"E8.0.9.0")])],"isStart":true})});
            var Q10;
            Q10=makeQuery(id+"F7.boolean.opBoolean","COPY",EDGE,{"derivedFrom":makeQuery(id+"F7.opExtrude","CAP_EDGE",EDGE,{"disambiguationData":[OSD([sQuery(id+"F6.wireOp",EDGE,"E8.0.10.0")])],"isStart":true})});
            var Q11;
            Q11=makeQuery(id+"F7.boolean.opBoolean","COPY",EDGE,{"derivedFrom":makeQuery(id+"F7.opExtrude","CAP_EDGE",EDGE,{"disambiguationData":[OSD([sQuery(id+"F6.wireOp",EDGE,"E8.0.11.0")])],"isStart":true})});
            var Q12;
            Q12=makeQuery(id+"F7.boolean.opBoolean","COPY",EDGE,{"derivedFrom":makeQuery(id+"F7.opExtrude","CAP_EDGE",EDGE,{"disambiguationData":[OSD([sQuery(id+"F6.wireOp",EDGE,"E8.0.12.0")])],"isStart":true})});
            var Q13;
            Q13=makeQuery(id+"F7.boolean.opBoolean","COPY",EDGE,{"derivedFrom":makeQuery(id+"F7.opExtrude","CAP_EDGE",EDGE,{"disambiguationData":[OSD([sQuery(id+"F6.wireOp",EDGE,"E8.0.13.0")])],"isStart":true})});
            var Q14;
            Q14=makeQuery(id+"F7.boolean.opBoolean","COPY",EDGE,{"derivedFrom":makeQuery(id+"F7.opExtrude","CAP_EDGE",EDGE,{"disambiguationData":[OSD([sQuery(id+"F6.wireOp",EDGE,"E8.0.14.0")])],"isStart":true})});
            var Q15;
            Q15=makeQuery(id+"F7.boolean.opBoolean","COPY",EDGE,{"derivedFrom":makeQuery(id+"F7.opExtrude","CAP_EDGE",EDGE,{"disambiguationData":[OSD([sQuery(id+"F6.wireOp",EDGE,"E9.0.0.15")])],"isStart":true})});
            var Q16;
            Q16=makeQuery(id+"F7.boolean.opBoolean","COPY",EDGE,{"derivedFrom":makeQuery(id+"F7.opExtrude","CAP_EDGE",EDGE,{"disambiguationData":[OSD([sQuery(id+"F6.wireOp",EDGE,"E9.0.0.16")])],"isStart":true})});
            var Q17;
            Q17=makeQuery(id+"F7.boolean.opBoolean","COPY",EDGE,{"derivedFrom":makeQuery(id+"F7.opExtrude","CAP_EDGE",EDGE,{"disambiguationData":[OSD([sQuery(id+"F6.wireOp",EDGE,"E9.0.0.17")])],"isStart":true})});
            var Q18;
            Q18=makeQuery(id+"F7.boolean.opBoolean","COPY",EDGE,{"derivedFrom":makeQuery(id+"F7.opExtrude","CAP_EDGE",EDGE,{"disambiguationData":[OSD([sQuery(id+"F6.wireOp",EDGE,"E9.0.0.18")])],"isStart":true})});
            var Q19;
            Q19=makeQuery(id+"F7.boolean.opBoolean","COPY",EDGE,{"derivedFrom":makeQuery(id+"F7.opExtrude","CAP_EDGE",EDGE,{"disambiguationData":[OSD([sQuery(id+"F6.wireOp",EDGE,"E9.0.0.19")])],"isStart":true})});
            var Q20;
            Q20=makeQuery(id+"F7.boolean.opBoolean","COPY",EDGE,{"derivedFrom":makeQuery(id+"F7.opExtrude","CAP_EDGE",EDGE,{"disambiguationData":[OSD([sQuery(id+"F6.wireOp",EDGE,"E9.0.7.19")])],"isStart":true})});
            var Q21;
            Q21=makeQuery(id+"F7.boolean.opBoolean","COPY",EDGE,{"derivedFrom":makeQuery(id+"F7.opExtrude","CAP_EDGE",EDGE,{"disambiguationData":[OSD([sQuery(id+"F6.wireOp",EDGE,"E9.0.7.18")])],"isStart":true})});
            var Q22;
            Q22=makeQuery(id+"F7.boolean.opBoolean","COPY",EDGE,{"derivedFrom":makeQuery(id+"F7.opExtrude","CAP_EDGE",EDGE,{"disambiguationData":[OSD([sQuery(id+"F6.wireOp",EDGE,"E9.0.7.17")])],"isStart":true})});
            var Q23;
            Q23=makeQuery(id+"F7.boolean.opBoolean","COPY",EDGE,{"derivedFrom":makeQuery(id+"F7.opExtrude","CAP_EDGE",EDGE,{"disambiguationData":[OSD([sQuery(id+"F6.wireOp",EDGE,"E9.0.7.16")])],"isStart":true})});
            var Q24;
            Q24=makeQuery(id+"F7.boolean.opBoolean","COPY",EDGE,{"derivedFrom":makeQuery(id+"F7.opExtrude","CAP_EDGE",EDGE,{"disambiguationData":[OSD([sQuery(id+"F6.wireOp",EDGE,"E9.0.7.15")])],"isStart":true})});
            var Q25;
            Q25=makeQuery(id+"F7.boolean.opBoolean","COPY",EDGE,{"derivedFrom":makeQuery(id+"F7.opExtrude","CAP_EDGE",EDGE,{"disambiguationData":[OSD([sQuery(id+"F6.wireOp",EDGE,"E9.0.6.19")])],"isStart":true})});
            var Q26;
            Q26=makeQuery(id+"F7.boolean.opBoolean","COPY",EDGE,{"derivedFrom":makeQuery(id+"F7.opExtrude","CAP_EDGE",EDGE,{"disambiguationData":[OSD([sQuery(id+"F6.wireOp",EDGE,"E9.0.6.18")])],"isStart":true})});
            var Q27;
            Q27=makeQuery(id+"F7.boolean.opBoolean","COPY",EDGE,{"derivedFrom":makeQuery(id+"F7.opExtrude","CAP_EDGE",EDGE,{"disambiguationData":[OSD([sQuery(id+"F6.wireOp",EDGE,"E9.0.6.17")])],"isStart":true})});
            var Q28;
            Q28=makeQuery(id+"F7.boolean.opBoolean","COPY",EDGE,{"derivedFrom":makeQuery(id+"F7.opExtrude","CAP_EDGE",EDGE,{"disambiguationData":[OSD([sQuery(id+"F6.wireOp",EDGE,"E9.0.6.16")])],"isStart":true})});
            var Q29;
            Q29=makeQuery(id+"F7.boolean.opBoolean","COPY",EDGE,{"derivedFrom":makeQuery(id+"F7.opExtrude","CAP_EDGE",EDGE,{"disambiguationData":[OSD([sQuery(id+"F6.wireOp",EDGE,"E9.0.6.15")])],"isStart":true})});
            var Q30;
            Q30=makeQuery(id+"F7.boolean.opBoolean","COPY",EDGE,{"derivedFrom":makeQuery(id+"F7.opExtrude","CAP_EDGE",EDGE,{"disambiguationData":[OSD([sQuery(id+"F6.wireOp",EDGE,"E9.0.5.19")])],"isStart":true})});
            var Q31;
            Q31=makeQuery(id+"F7.boolean.opBoolean","COPY",EDGE,{"derivedFrom":makeQuery(id+"F7.opExtrude","CAP_EDGE",EDGE,{"disambiguationData":[OSD([sQuery(id+"F6.wireOp",EDGE,"E9.0.5.18")])],"isStart":true})});
            var Q32;
            Q32=makeQuery(id+"F7.boolean.opBoolean","COPY",EDGE,{"derivedFrom":makeQuery(id+"F7.opExtrude","CAP_EDGE",EDGE,{"disambiguationData":[OSD([sQuery(id+"F6.wireOp",EDGE,"E9.0.5.17")])],"isStart":true})});
            var Q33;
            Q33=makeQuery(id+"F7.boolean.opBoolean","COPY",EDGE,{"derivedFrom":makeQuery(id+"F7.opExtrude","CAP_EDGE",EDGE,{"disambiguationData":[OSD([sQuery(id+"F6.wireOp",EDGE,"E9.0.5.16")])],"isStart":true})});
            var Q34;
            Q34=makeQuery(id+"F7.boolean.opBoolean","COPY",EDGE,{"derivedFrom":makeQuery(id+"F7.opExtrude","CAP_EDGE",EDGE,{"disambiguationData":[OSD([sQuery(id+"F6.wireOp",EDGE,"E9.0.5.15")])],"isStart":true})});
            var Q35;
            Q35=makeQuery(id+"F7.boolean.opBoolean","COPY",EDGE,{"derivedFrom":makeQuery(id+"F7.opExtrude","CAP_EDGE",EDGE,{"disambiguationData":[OSD([sQuery(id+"F6.wireOp",EDGE,"E9.0.4.19")])],"isStart":true})});
            var Q36;
            Q36=makeQuery(id+"F7.boolean.opBoolean","COPY",EDGE,{"derivedFrom":makeQuery(id+"F7.opExtrude","CAP_EDGE",EDGE,{"disambiguationData":[OSD([sQuery(id+"F6.wireOp",EDGE,"E9.0.4.18")])],"isStart":true})});
            var Q37;
            Q37=makeQuery(id+"F7.boolean.opBoolean","COPY",EDGE,{"derivedFrom":makeQuery(id+"F7.opExtrude","CAP_EDGE",EDGE,{"disambiguationData":[OSD([sQuery(id+"F6.wireOp",EDGE,"E9.0.4.17")])],"isStart":true})});
            var Q38;
            Q38=makeQuery(id+"F7.boolean.opBoolean","COPY",EDGE,{"derivedFrom":makeQuery(id+"F7.opExtrude","CAP_EDGE",EDGE,{"disambiguationData":[OSD([sQuery(id+"F6.wireOp",EDGE,"E9.0.4.16")])],"isStart":true})});
            var Q39;
            Q39=makeQuery(id+"F7.boolean.opBoolean","COPY",EDGE,{"derivedFrom":makeQuery(id+"F7.opExtrude","CAP_EDGE",EDGE,{"disambiguationData":[OSD([sQuery(id+"F6.wireOp",EDGE,"E9.0.4.15")])],"isStart":true})});
            var Q40;
            Q40=makeQuery(id+"F7.boolean.opBoolean","COPY",EDGE,{"derivedFrom":makeQuery(id+"F7.opExtrude","CAP_EDGE",EDGE,{"disambiguationData":[OSD([sQuery(id+"F6.wireOp",EDGE,"E9.0.3.19")])],"isStart":true})});
            var Q41;
            Q41=makeQuery(id+"F7.boolean.opBoolean","COPY",EDGE,{"derivedFrom":makeQuery(id+"F7.opExtrude","CAP_EDGE",EDGE,{"disambiguationData":[OSD([sQuery(id+"F6.wireOp",EDGE,"E9.0.3.18")])],"isStart":true})});
            var Q42;
            Q42=makeQuery(id+"F7.boolean.opBoolean","COPY",EDGE,{"derivedFrom":makeQuery(id+"F7.opExtrude","CAP_EDGE",EDGE,{"disambiguationData":[OSD([sQuery(id+"F6.wireOp",EDGE,"E9.0.3.17")])],"isStart":true})});
            var Q43;
            Q43=makeQuery(id+"F7.boolean.opBoolean","COPY",EDGE,{"derivedFrom":makeQuery(id+"F7.opExtrude","CAP_EDGE",EDGE,{"disambiguationData":[OSD([sQuery(id+"F6.wireOp",EDGE,"E9.0.3.16")])],"isStart":true})});
            var Q44;
            Q44=makeQuery(id+"F7.boolean.opBoolean","COPY",EDGE,{"derivedFrom":makeQuery(id+"F7.opExtrude","CAP_EDGE",EDGE,{"disambiguationData":[OSD([sQuery(id+"F6.wireOp",EDGE,"E9.0.3.15")])],"isStart":true})});
            var Q45;
            Q45=makeQuery(id+"F7.boolean.opBoolean","COPY",EDGE,{"derivedFrom":makeQuery(id+"F7.opExtrude","CAP_EDGE",EDGE,{"disambiguationData":[OSD([sQuery(id+"F6.wireOp",EDGE,"E9.0.2.19")])],"isStart":true})});
            var Q46;
            Q46=makeQuery(id+"F7.boolean.opBoolean","COPY",EDGE,{"derivedFrom":makeQuery(id+"F7.opExtrude","CAP_EDGE",EDGE,{"disambiguationData":[OSD([sQuery(id+"F6.wireOp",EDGE,"E9.0.2.18")])],"isStart":true})});
            var Q47;
            Q47=makeQuery(id+"F7.boolean.opBoolean","COPY",EDGE,{"derivedFrom":makeQuery(id+"F7.opExtrude","CAP_EDGE",EDGE,{"disambiguationData":[OSD([sQuery(id+"F6.wireOp",EDGE,"E9.0.2.17")])],"isStart":true})});
            var Q48;
            Q48=makeQuery(id+"F7.boolean.opBoolean","COPY",EDGE,{"derivedFrom":makeQuery(id+"F7.opExtrude","CAP_EDGE",EDGE,{"disambiguationData":[OSD([sQuery(id+"F6.wireOp",EDGE,"E9.0.2.16")])],"isStart":true})});
            var Q49;
            Q49=makeQuery(id+"F7.boolean.opBoolean","COPY",EDGE,{"derivedFrom":makeQuery(id+"F7.opExtrude","CAP_EDGE",EDGE,{"disambiguationData":[OSD([sQuery(id+"F6.wireOp",EDGE,"E9.0.2.15")])],"isStart":true})});
            var Q50;
            Q50=makeQuery(id+"F7.boolean.opBoolean","COPY",EDGE,{"derivedFrom":makeQuery(id+"F7.opExtrude","CAP_EDGE",EDGE,{"disambiguationData":[OSD([sQuery(id+"F6.wireOp",EDGE,"E9.0.1.19")])],"isStart":true})});
            var Q51;
            Q51=makeQuery(id+"F7.boolean.opBoolean","COPY",EDGE,{"derivedFrom":makeQuery(id+"F7.opExtrude","CAP_EDGE",EDGE,{"disambiguationData":[OSD([sQuery(id+"F6.wireOp",EDGE,"E9.0.1.18")])],"isStart":true})});
            var Q52;
            Q52=makeQuery(id+"F7.boolean.opBoolean","COPY",EDGE,{"derivedFrom":makeQuery(id+"F7.opExtrude","CAP_EDGE",EDGE,{"disambiguationData":[OSD([sQuery(id+"F6.wireOp",EDGE,"E9.0.1.17")])],"isStart":true})});
            var Q53;
            Q53=makeQuery(id+"F7.boolean.opBoolean","COPY",EDGE,{"derivedFrom":makeQuery(id+"F7.opExtrude","CAP_EDGE",EDGE,{"disambiguationData":[OSD([sQuery(id+"F6.wireOp",EDGE,"E9.0.1.16")])],"isStart":true})});
            var Q54;
            Q54=makeQuery(id+"F7.boolean.opBoolean","COPY",EDGE,{"derivedFrom":makeQuery(id+"F7.opExtrude","CAP_EDGE",EDGE,{"disambiguationData":[OSD([sQuery(id+"F6.wireOp",EDGE,"E9.0.1.15")])],"isStart":true})});
            var Q55;
            Q55=makeQuery(id+"F7.boolean.opBoolean","COPY",EDGE,{"derivedFrom":makeQuery(id+"F7.opExtrude","CAP_EDGE",EDGE,{"disambiguationData":[OSD([sQuery(id+"F6.wireOp",EDGE,"E8.8.14.0")])],"isStart":true})});
            var Q56;
            Q56=makeQuery(id+"F7.boolean.opBoolean","COPY",EDGE,{"derivedFrom":makeQuery(id+"F7.opExtrude","CAP_EDGE",EDGE,{"disambiguationData":[OSD([sQuery(id+"F6.wireOp",EDGE,"E8.8.13.0")])],"isStart":true})});
            var Q57;
            Q57=makeQuery(id+"F7.boolean.opBoolean","COPY",EDGE,{"derivedFrom":makeQuery(id+"F7.opExtrude","CAP_EDGE",EDGE,{"disambiguationData":[OSD([sQuery(id+"F6.wireOp",EDGE,"E8.8.12.0")])],"isStart":true})});
            var Q58;
            Q58=makeQuery(id+"F7.boolean.opBoolean","COPY",EDGE,{"derivedFrom":makeQuery(id+"F7.opExtrude","CAP_EDGE",EDGE,{"disambiguationData":[OSD([sQuery(id+"F6.wireOp",EDGE,"E8.8.11.0")])],"isStart":true})});
            var Q59;
            Q59=makeQuery(id+"F7.boolean.opBoolean","COPY",EDGE,{"derivedFrom":makeQuery(id+"F7.opExtrude","CAP_EDGE",EDGE,{"disambiguationData":[OSD([sQuery(id+"F6.wireOp",EDGE,"E8.8.10.0")])],"isStart":true})});
            var Q60;
            Q60=makeQuery(id+"F7.boolean.opBoolean","COPY",EDGE,{"derivedFrom":makeQuery(id+"F7.opExtrude","CAP_EDGE",EDGE,{"disambiguationData":[OSD([sQuery(id+"F6.wireOp",EDGE,"E8.8.9.0")])],"isStart":true})});
            var Q61;
            Q61=makeQuery(id+"F7.boolean.opBoolean","COPY",EDGE,{"derivedFrom":makeQuery(id+"F7.opExtrude","CAP_EDGE",EDGE,{"disambiguationData":[OSD([sQuery(id+"F6.wireOp",EDGE,"E8.8.8.0")])],"isStart":true})});
            var Q62;
            Q62=makeQuery(id+"F7.boolean.opBoolean","COPY",EDGE,{"derivedFrom":makeQuery(id+"F7.opExtrude","CAP_EDGE",EDGE,{"disambiguationData":[OSD([sQuery(id+"F6.wireOp",EDGE,"E8.8.7.0")])],"isStart":true})});
            var Q63;
            Q63=makeQuery(id+"F7.boolean.opBoolean","COPY",EDGE,{"derivedFrom":makeQuery(id+"F7.opExtrude","CAP_EDGE",EDGE,{"disambiguationData":[OSD([sQuery(id+"F6.wireOp",EDGE,"E8.8.6.0")])],"isStart":true})});
            var Q64;
            Q64=makeQuery(id+"F7.boolean.opBoolean","COPY",EDGE,{"derivedFrom":makeQuery(id+"F7.opExtrude","CAP_EDGE",EDGE,{"disambiguationData":[OSD([sQuery(id+"F6.wireOp",EDGE,"E8.8.5.0")])],"isStart":true})});
            var Q65;
            Q65=makeQuery(id+"F7.boolean.opBoolean","COPY",EDGE,{"derivedFrom":makeQuery(id+"F7.opExtrude","CAP_EDGE",EDGE,{"disambiguationData":[OSD([sQuery(id+"F6.wireOp",EDGE,"E8.8.4.0")])],"isStart":true})});
            var Q66;
            Q66=makeQuery(id+"F7.boolean.opBoolean","COPY",EDGE,{"derivedFrom":makeQuery(id+"F7.opExtrude","CAP_EDGE",EDGE,{"disambiguationData":[OSD([sQuery(id+"F6.wireOp",EDGE,"E8.8.3.0")])],"isStart":true})});
            var Q67;
            Q67=makeQuery(id+"F7.boolean.opBoolean","COPY",EDGE,{"derivedFrom":makeQuery(id+"F7.opExtrude","CAP_EDGE",EDGE,{"disambiguationData":[OSD([sQuery(id+"F6.wireOp",EDGE,"E8.8.2.0")])],"isStart":true})});
            var Q68;
            Q68=makeQuery(id+"F7.boolean.opBoolean","COPY",EDGE,{"derivedFrom":makeQuery(id+"F7.opExtrude","CAP_EDGE",EDGE,{"disambiguationData":[OSD([sQuery(id+"F6.wireOp",EDGE,"E8.8.1.0")])],"isStart":true})});
            var Q69;
            Q69=makeQuery(id+"F7.boolean.opBoolean","COPY",EDGE,{"derivedFrom":makeQuery(id+"F7.opExtrude","CAP_EDGE",EDGE,{"disambiguationData":[OSD([sQuery(id+"F6.wireOp",EDGE,"E8.8.0.0")])],"isStart":true})});
            var Q70;
            Q70=makeQuery(id+"F7.boolean.opBoolean","COPY",EDGE,{"derivedFrom":makeQuery(id+"F7.opExtrude","CAP_EDGE",EDGE,{"disambiguationData":[OSD([sQuery(id+"F6.wireOp",EDGE,"E8.7.14.0")])],"isStart":true})});
            var Q71;
            Q71=makeQuery(id+"F7.boolean.opBoolean","COPY",EDGE,{"derivedFrom":makeQuery(id+"F7.opExtrude","CAP_EDGE",EDGE,{"disambiguationData":[OSD([sQuery(id+"F6.wireOp",EDGE,"E8.7.13.0")])],"isStart":true})});
            var Q72;
            Q72=makeQuery(id+"F7.boolean.opBoolean","COPY",EDGE,{"derivedFrom":makeQuery(id+"F7.opExtrude","CAP_EDGE",EDGE,{"disambiguationData":[OSD([sQuery(id+"F6.wireOp",EDGE,"E8.7.12.0")])],"isStart":true})});
            var Q73;
            Q73=makeQuery(id+"F7.boolean.opBoolean","COPY",EDGE,{"derivedFrom":makeQuery(id+"F7.opExtrude","CAP_EDGE",EDGE,{"disambiguationData":[OSD([sQuery(id+"F6.wireOp",EDGE,"E8.7.11.0")])],"isStart":true})});
            var Q74;
            Q74=makeQuery(id+"F7.boolean.opBoolean","COPY",EDGE,{"derivedFrom":makeQuery(id+"F7.opExtrude","CAP_EDGE",EDGE,{"disambiguationData":[OSD([sQuery(id+"F6.wireOp",EDGE,"E8.7.10.0")])],"isStart":true})});
            var Q75;
            Q75=makeQuery(id+"F7.boolean.opBoolean","COPY",EDGE,{"derivedFrom":makeQuery(id+"F7.opExtrude","CAP_EDGE",EDGE,{"disambiguationData":[OSD([sQuery(id+"F6.wireOp",EDGE,"E8.7.9.0")])],"isStart":true})});
            var Q76;
            Q76=makeQuery(id+"F7.boolean.opBoolean","COPY",EDGE,{"derivedFrom":makeQuery(id+"F7.opExtrude","CAP_EDGE",EDGE,{"disambiguationData":[OSD([sQuery(id+"F6.wireOp",EDGE,"E8.7.8.0")])],"isStart":true})});
            var Q77;
            Q77=makeQuery(id+"F7.boolean.opBoolean","COPY",EDGE,{"derivedFrom":makeQuery(id+"F7.opExtrude","CAP_EDGE",EDGE,{"disambiguationData":[OSD([sQuery(id+"F6.wireOp",EDGE,"E8.7.7.0")])],"isStart":true})});
            var Q78;
            Q78=makeQuery(id+"F7.boolean.opBoolean","COPY",EDGE,{"derivedFrom":makeQuery(id+"F7.opExtrude","CAP_EDGE",EDGE,{"disambiguationData":[OSD([sQuery(id+"F6.wireOp",EDGE,"E8.7.6.0")])],"isStart":true})});
            var Q79;
            Q79=makeQuery(id+"F7.boolean.opBoolean","COPY",EDGE,{"derivedFrom":makeQuery(id+"F7.opExtrude","CAP_EDGE",EDGE,{"disambiguationData":[OSD([sQuery(id+"F6.wireOp",EDGE,"E8.7.5.0")])],"isStart":true})});
            var Q80;
            Q80=makeQuery(id+"F7.boolean.opBoolean","COPY",EDGE,{"derivedFrom":makeQuery(id+"F7.opExtrude","CAP_EDGE",EDGE,{"disambiguationData":[OSD([sQuery(id+"F6.wireOp",EDGE,"E8.7.4.0")])],"isStart":true})});
            var Q81;
            Q81=makeQuery(id+"F7.boolean.opBoolean","COPY",EDGE,{"derivedFrom":makeQuery(id+"F7.opExtrude","CAP_EDGE",EDGE,{"disambiguationData":[OSD([sQuery(id+"F6.wireOp",EDGE,"E8.7.3.0")])],"isStart":true})});
            var Q82;
            Q82=makeQuery(id+"F7.boolean.opBoolean","COPY",EDGE,{"derivedFrom":makeQuery(id+"F7.opExtrude","CAP_EDGE",EDGE,{"disambiguationData":[OSD([sQuery(id+"F6.wireOp",EDGE,"E8.7.2.0")])],"isStart":true})});
            var Q83;
            Q83=makeQuery(id+"F7.boolean.opBoolean","COPY",EDGE,{"derivedFrom":makeQuery(id+"F7.opExtrude","CAP_EDGE",EDGE,{"disambiguationData":[OSD([sQuery(id+"F6.wireOp",EDGE,"E8.7.1.0")])],"isStart":true})});
            var Q84;
            Q84=makeQuery(id+"F7.boolean.opBoolean","COPY",EDGE,{"derivedFrom":makeQuery(id+"F7.opExtrude","CAP_EDGE",EDGE,{"disambiguationData":[OSD([sQuery(id+"F6.wireOp",EDGE,"E8.7.0.0")])],"isStart":true})});
            var Q85;
            Q85=makeQuery(id+"F7.boolean.opBoolean","COPY",EDGE,{"derivedFrom":makeQuery(id+"F7.opExtrude","CAP_EDGE",EDGE,{"disambiguationData":[OSD([sQuery(id+"F6.wireOp",EDGE,"E8.6.14.0")])],"isStart":true})});
            var Q86;
            Q86=makeQuery(id+"F7.boolean.opBoolean","COPY",EDGE,{"derivedFrom":makeQuery(id+"F7.opExtrude","CAP_EDGE",EDGE,{"disambiguationData":[OSD([sQuery(id+"F6.wireOp",EDGE,"E8.6.13.0")])],"isStart":true})});
            var Q87;
            Q87=makeQuery(id+"F7.boolean.opBoolean","COPY",EDGE,{"derivedFrom":makeQuery(id+"F7.opExtrude","CAP_EDGE",EDGE,{"disambiguationData":[OSD([sQuery(id+"F6.wireOp",EDGE,"E8.6.12.0")])],"isStart":true})});
            var Q88;
            Q88=makeQuery(id+"F7.boolean.opBoolean","COPY",EDGE,{"derivedFrom":makeQuery(id+"F7.opExtrude","CAP_EDGE",EDGE,{"disambiguationData":[OSD([sQuery(id+"F6.wireOp",EDGE,"E8.6.11.0")])],"isStart":true})});
            var Q89;
            Q89=makeQuery(id+"F7.boolean.opBoolean","COPY",EDGE,{"derivedFrom":makeQuery(id+"F7.opExtrude","CAP_EDGE",EDGE,{"disambiguationData":[OSD([sQuery(id+"F6.wireOp",EDGE,"E8.6.10.0")])],"isStart":true})});
            var Q90;
            Q90=makeQuery(id+"F7.boolean.opBoolean","COPY",EDGE,{"derivedFrom":makeQuery(id+"F7.opExtrude","CAP_EDGE",EDGE,{"disambiguationData":[OSD([sQuery(id+"F6.wireOp",EDGE,"E8.6.9.0")])],"isStart":true})});
            var Q91;
            Q91=makeQuery(id+"F7.boolean.opBoolean","COPY",EDGE,{"derivedFrom":makeQuery(id+"F7.opExtrude","CAP_EDGE",EDGE,{"disambiguationData":[OSD([sQuery(id+"F6.wireOp",EDGE,"E8.6.8.0")])],"isStart":true})});
            var Q92;
            Q92=makeQuery(id+"F7.boolean.opBoolean","COPY",EDGE,{"derivedFrom":makeQuery(id+"F7.opExtrude","CAP_EDGE",EDGE,{"disambiguationData":[OSD([sQuery(id+"F6.wireOp",EDGE,"E8.6.7.0")])],"isStart":true})});
            var Q93;
            Q93=makeQuery(id+"F7.boolean.opBoolean","COPY",EDGE,{"derivedFrom":makeQuery(id+"F7.opExtrude","CAP_EDGE",EDGE,{"disambiguationData":[OSD([sQuery(id+"F6.wireOp",EDGE,"E8.6.6.0")])],"isStart":true})});
            var Q94;
            Q94=makeQuery(id+"F7.boolean.opBoolean","COPY",EDGE,{"derivedFrom":makeQuery(id+"F7.opExtrude","CAP_EDGE",EDGE,{"disambiguationData":[OSD([sQuery(id+"F6.wireOp",EDGE,"E8.6.5.0")])],"isStart":true})});
            var Q95;
            Q95=makeQuery(id+"F7.boolean.opBoolean","COPY",EDGE,{"derivedFrom":makeQuery(id+"F7.opExtrude","CAP_EDGE",EDGE,{"disambiguationData":[OSD([sQuery(id+"F6.wireOp",EDGE,"E8.6.4.0")])],"isStart":true})});
            var Q96;
            Q96=makeQuery(id+"F7.boolean.opBoolean","COPY",EDGE,{"derivedFrom":makeQuery(id+"F7.opExtrude","CAP_EDGE",EDGE,{"disambiguationData":[OSD([sQuery(id+"F6.wireOp",EDGE,"E8.6.3.0")])],"isStart":true})});
            var Q97;
            Q97=makeQuery(id+"F7.boolean.opBoolean","COPY",EDGE,{"derivedFrom":makeQuery(id+"F7.opExtrude","CAP_EDGE",EDGE,{"disambiguationData":[OSD([sQuery(id+"F6.wireOp",EDGE,"E8.6.2.0")])],"isStart":true})});
            var Q98;
            Q98=makeQuery(id+"F7.boolean.opBoolean","COPY",EDGE,{"derivedFrom":makeQuery(id+"F7.opExtrude","CAP_EDGE",EDGE,{"disambiguationData":[OSD([sQuery(id+"F6.wireOp",EDGE,"E8.6.1.0")])],"isStart":true})});
            var Q99;
            Q99=makeQuery(id+"F7.boolean.opBoolean","COPY",EDGE,{"derivedFrom":makeQuery(id+"F7.opExtrude","CAP_EDGE",EDGE,{"disambiguationData":[OSD([sQuery(id+"F6.wireOp",EDGE,"E8.6.0.0")])],"isStart":true})});
            var Q100;
            Q100=makeQuery(id+"F7.boolean.opBoolean","COPY",EDGE,{"derivedFrom":makeQuery(id+"F7.opExtrude","CAP_EDGE",EDGE,{"disambiguationData":[OSD([sQuery(id+"F6.wireOp",EDGE,"E8.5.14.0")])],"isStart":true})});
            var Q101;
            Q101=makeQuery(id+"F7.boolean.opBoolean","COPY",EDGE,{"derivedFrom":makeQuery(id+"F7.opExtrude","CAP_EDGE",EDGE,{"disambiguationData":[OSD([sQuery(id+"F6.wireOp",EDGE,"E8.5.13.0")])],"isStart":true})});
            var Q102;
            Q102=makeQuery(id+"F7.boolean.opBoolean","COPY",EDGE,{"derivedFrom":makeQuery(id+"F7.opExtrude","CAP_EDGE",EDGE,{"disambiguationData":[OSD([sQuery(id+"F6.wireOp",EDGE,"E8.5.12.0")])],"isStart":true})});
            var Q103;
            Q103=makeQuery(id+"F7.boolean.opBoolean","COPY",EDGE,{"derivedFrom":makeQuery(id+"F7.opExtrude","CAP_EDGE",EDGE,{"disambiguationData":[OSD([sQuery(id+"F6.wireOp",EDGE,"E8.5.11.0")])],"isStart":true})});
            var Q104;
            Q104=makeQuery(id+"F7.boolean.opBoolean","COPY",EDGE,{"derivedFrom":makeQuery(id+"F7.opExtrude","CAP_EDGE",EDGE,{"disambiguationData":[OSD([sQuery(id+"F6.wireOp",EDGE,"E8.5.10.0")])],"isStart":true})});
            var Q105;
            Q105=makeQuery(id+"F7.boolean.opBoolean","COPY",EDGE,{"derivedFrom":makeQuery(id+"F7.opExtrude","CAP_EDGE",EDGE,{"disambiguationData":[OSD([sQuery(id+"F6.wireOp",EDGE,"E8.5.9.0")])],"isStart":true})});
            var Q106;
            Q106=makeQuery(id+"F7.boolean.opBoolean","COPY",EDGE,{"derivedFrom":makeQuery(id+"F7.opExtrude","CAP_EDGE",EDGE,{"disambiguationData":[OSD([sQuery(id+"F6.wireOp",EDGE,"E8.5.8.0")])],"isStart":true})});
            var Q107;
            Q107=makeQuery(id+"F7.boolean.opBoolean","COPY",EDGE,{"derivedFrom":makeQuery(id+"F7.opExtrude","CAP_EDGE",EDGE,{"disambiguationData":[OSD([sQuery(id+"F6.wireOp",EDGE,"E8.5.7.0")])],"isStart":true})});
            var Q108;
            Q108=makeQuery(id+"F7.boolean.opBoolean","COPY",EDGE,{"derivedFrom":makeQuery(id+"F7.opExtrude","CAP_EDGE",EDGE,{"disambiguationData":[OSD([sQuery(id+"F6.wireOp",EDGE,"E8.5.6.0")])],"isStart":true})});
            var Q109;
            Q109=makeQuery(id+"F7.boolean.opBoolean","COPY",EDGE,{"derivedFrom":makeQuery(id+"F7.opExtrude","CAP_EDGE",EDGE,{"disambiguationData":[OSD([sQuery(id+"F6.wireOp",EDGE,"E8.5.5.0")])],"isStart":true})});
            var Q110;
            Q110=makeQuery(id+"F7.boolean.opBoolean","COPY",EDGE,{"derivedFrom":makeQuery(id+"F7.opExtrude","CAP_EDGE",EDGE,{"disambiguationData":[OSD([sQuery(id+"F6.wireOp",EDGE,"E8.5.4.0")])],"isStart":true})});
            var Q111;
            Q111=makeQuery(id+"F7.boolean.opBoolean","COPY",EDGE,{"derivedFrom":makeQuery(id+"F7.opExtrude","CAP_EDGE",EDGE,{"disambiguationData":[OSD([sQuery(id+"F6.wireOp",EDGE,"E8.5.3.0")])],"isStart":true})});
            var Q112;
            Q112=makeQuery(id+"F7.boolean.opBoolean","COPY",EDGE,{"derivedFrom":makeQuery(id+"F7.opExtrude","CAP_EDGE",EDGE,{"disambiguationData":[OSD([sQuery(id+"F6.wireOp",EDGE,"E8.5.2.0")])],"isStart":true})});
            var Q113;
            Q113=makeQuery(id+"F7.boolean.opBoolean","COPY",EDGE,{"derivedFrom":makeQuery(id+"F7.opExtrude","CAP_EDGE",EDGE,{"disambiguationData":[OSD([sQuery(id+"F6.wireOp",EDGE,"E8.5.1.0")])],"isStart":true})});
            var Q114;
            Q114=makeQuery(id+"F7.boolean.opBoolean","COPY",EDGE,{"derivedFrom":makeQuery(id+"F7.opExtrude","CAP_EDGE",EDGE,{"disambiguationData":[OSD([sQuery(id+"F6.wireOp",EDGE,"E8.5.0.0")])],"isStart":true})});
            var Q115;
            Q115=makeQuery(id+"F7.boolean.opBoolean","COPY",EDGE,{"derivedFrom":makeQuery(id+"F7.opExtrude","CAP_EDGE",EDGE,{"disambiguationData":[OSD([sQuery(id+"F6.wireOp",EDGE,"E8.4.14.0")])],"isStart":true})});
            var Q116;
            Q116=makeQuery(id+"F7.boolean.opBoolean","COPY",EDGE,{"derivedFrom":makeQuery(id+"F7.opExtrude","CAP_EDGE",EDGE,{"disambiguationData":[OSD([sQuery(id+"F6.wireOp",EDGE,"E8.4.13.0")])],"isStart":true})});
            var Q117;
            Q117=makeQuery(id+"F7.boolean.opBoolean","COPY",EDGE,{"derivedFrom":makeQuery(id+"F7.opExtrude","CAP_EDGE",EDGE,{"disambiguationData":[OSD([sQuery(id+"F6.wireOp",EDGE,"E8.4.12.0")])],"isStart":true})});
            var Q118;
            Q118=makeQuery(id+"F7.boolean.opBoolean","COPY",EDGE,{"derivedFrom":makeQuery(id+"F7.opExtrude","CAP_EDGE",EDGE,{"disambiguationData":[OSD([sQuery(id+"F6.wireOp",EDGE,"E8.4.11.0")])],"isStart":true})});
            var Q119;
            Q119=makeQuery(id+"F7.boolean.opBoolean","COPY",EDGE,{"derivedFrom":makeQuery(id+"F7.opExtrude","CAP_EDGE",EDGE,{"disambiguationData":[OSD([sQuery(id+"F6.wireOp",EDGE,"E8.4.10.0")])],"isStart":true})});
            var Q120;
            Q120=makeQuery(id+"F7.boolean.opBoolean","COPY",EDGE,{"derivedFrom":makeQuery(id+"F7.opExtrude","CAP_EDGE",EDGE,{"disambiguationData":[OSD([sQuery(id+"F6.wireOp",EDGE,"E8.4.9.0")])],"isStart":true})});
            var Q121;
            Q121=makeQuery(id+"F7.boolean.opBoolean","COPY",EDGE,{"derivedFrom":makeQuery(id+"F7.opExtrude","CAP_EDGE",EDGE,{"disambiguationData":[OSD([sQuery(id+"F6.wireOp",EDGE,"E8.4.8.0")])],"isStart":true})});
            var Q122;
            Q122=makeQuery(id+"F7.boolean.opBoolean","COPY",EDGE,{"derivedFrom":makeQuery(id+"F7.opExtrude","CAP_EDGE",EDGE,{"disambiguationData":[OSD([sQuery(id+"F6.wireOp",EDGE,"E8.4.7.0")])],"isStart":true})});
            var Q123;
            Q123=makeQuery(id+"F7.boolean.opBoolean","COPY",EDGE,{"derivedFrom":makeQuery(id+"F7.opExtrude","CAP_EDGE",EDGE,{"disambiguationData":[OSD([sQuery(id+"F6.wireOp",EDGE,"E8.4.6.0")])],"isStart":true})});
            var Q124;
            Q124=makeQuery(id+"F7.boolean.opBoolean","COPY",EDGE,{"derivedFrom":makeQuery(id+"F7.opExtrude","CAP_EDGE",EDGE,{"disambiguationData":[OSD([sQuery(id+"F6.wireOp",EDGE,"E8.4.5.0")])],"isStart":true})});
            var Q125;
            Q125=makeQuery(id+"F7.boolean.opBoolean","COPY",EDGE,{"derivedFrom":makeQuery(id+"F7.opExtrude","CAP_EDGE",EDGE,{"disambiguationData":[OSD([sQuery(id+"F6.wireOp",EDGE,"E8.4.4.0")])],"isStart":true})});
            var Q126;
            Q126=makeQuery(id+"F7.boolean.opBoolean","COPY",EDGE,{"derivedFrom":makeQuery(id+"F7.opExtrude","CAP_EDGE",EDGE,{"disambiguationData":[OSD([sQuery(id+"F6.wireOp",EDGE,"E8.4.3.0")])],"isStart":true})});
            var Q127;
            Q127=makeQuery(id+"F7.boolean.opBoolean","COPY",EDGE,{"derivedFrom":makeQuery(id+"F7.opExtrude","CAP_EDGE",EDGE,{"disambiguationData":[OSD([sQuery(id+"F6.wireOp",EDGE,"E8.4.2.0")])],"isStart":true})});
            var Q128;
            Q128=makeQuery(id+"F7.boolean.opBoolean","COPY",EDGE,{"derivedFrom":makeQuery(id+"F7.opExtrude","CAP_EDGE",EDGE,{"disambiguationData":[OSD([sQuery(id+"F6.wireOp",EDGE,"E8.4.1.0")])],"isStart":true})});
            var Q129;
            Q129=makeQuery(id+"F7.boolean.opBoolean","COPY",EDGE,{"derivedFrom":makeQuery(id+"F7.opExtrude","CAP_EDGE",EDGE,{"disambiguationData":[OSD([sQuery(id+"F6.wireOp",EDGE,"E8.4.0.0")])],"isStart":true})});
            var Q130;
            Q130=makeQuery(id+"F7.boolean.opBoolean","COPY",EDGE,{"derivedFrom":makeQuery(id+"F7.opExtrude","CAP_EDGE",EDGE,{"disambiguationData":[OSD([sQuery(id+"F6.wireOp",EDGE,"E8.3.14.0")])],"isStart":true})});
            var Q131;
            Q131=makeQuery(id+"F7.boolean.opBoolean","COPY",EDGE,{"derivedFrom":makeQuery(id+"F7.opExtrude","CAP_EDGE",EDGE,{"disambiguationData":[OSD([sQuery(id+"F6.wireOp",EDGE,"E8.3.13.0")])],"isStart":true})});
            var Q132;
            Q132=makeQuery(id+"F7.boolean.opBoolean","COPY",EDGE,{"derivedFrom":makeQuery(id+"F7.opExtrude","CAP_EDGE",EDGE,{"disambiguationData":[OSD([sQuery(id+"F6.wireOp",EDGE,"E8.3.12.0")])],"isStart":true})});
            var Q133;
            Q133=makeQuery(id+"F7.boolean.opBoolean","COPY",EDGE,{"derivedFrom":makeQuery(id+"F7.opExtrude","CAP_EDGE",EDGE,{"disambiguationData":[OSD([sQuery(id+"F6.wireOp",EDGE,"E8.3.11.0")])],"isStart":true})});
            var Q134;
            Q134=makeQuery(id+"F7.boolean.opBoolean","COPY",EDGE,{"derivedFrom":makeQuery(id+"F7.opExtrude","CAP_EDGE",EDGE,{"disambiguationData":[OSD([sQuery(id+"F6.wireOp",EDGE,"E8.3.10.0")])],"isStart":true})});
            var Q135;
            Q135=makeQuery(id+"F7.boolean.opBoolean","COPY",EDGE,{"derivedFrom":makeQuery(id+"F7.opExtrude","CAP_EDGE",EDGE,{"disambiguationData":[OSD([sQuery(id+"F6.wireOp",EDGE,"E8.3.9.0")])],"isStart":true})});
            var Q136;
            Q136=makeQuery(id+"F7.boolean.opBoolean","COPY",EDGE,{"derivedFrom":makeQuery(id+"F7.opExtrude","CAP_EDGE",EDGE,{"disambiguationData":[OSD([sQuery(id+"F6.wireOp",EDGE,"E8.3.8.0")])],"isStart":true})});
            var Q137;
            Q137=makeQuery(id+"F7.boolean.opBoolean","COPY",EDGE,{"derivedFrom":makeQuery(id+"F7.opExtrude","CAP_EDGE",EDGE,{"disambiguationData":[OSD([sQuery(id+"F6.wireOp",EDGE,"E8.3.7.0")])],"isStart":true})});
            var Q138;
            Q138=makeQuery(id+"F7.boolean.opBoolean","COPY",EDGE,{"derivedFrom":makeQuery(id+"F7.opExtrude","CAP_EDGE",EDGE,{"disambiguationData":[OSD([sQuery(id+"F6.wireOp",EDGE,"E8.3.6.0")])],"isStart":true})});
            var Q139;
            Q139=makeQuery(id+"F7.boolean.opBoolean","COPY",EDGE,{"derivedFrom":makeQuery(id+"F7.opExtrude","CAP_EDGE",EDGE,{"disambiguationData":[OSD([sQuery(id+"F6.wireOp",EDGE,"E8.3.5.0")])],"isStart":true})});
            var Q140;
            Q140=makeQuery(id+"F7.boolean.opBoolean","COPY",EDGE,{"derivedFrom":makeQuery(id+"F7.opExtrude","CAP_EDGE",EDGE,{"disambiguationData":[OSD([sQuery(id+"F6.wireOp",EDGE,"E8.3.4.0")])],"isStart":true})});
            var Q141;
            Q141=makeQuery(id+"F7.boolean.opBoolean","COPY",EDGE,{"derivedFrom":makeQuery(id+"F7.opExtrude","CAP_EDGE",EDGE,{"disambiguationData":[OSD([sQuery(id+"F6.wireOp",EDGE,"E8.3.3.0")])],"isStart":true})});
            var Q142;
            Q142=makeQuery(id+"F7.boolean.opBoolean","COPY",EDGE,{"derivedFrom":makeQuery(id+"F7.opExtrude","CAP_EDGE",EDGE,{"disambiguationData":[OSD([sQuery(id+"F6.wireOp",EDGE,"E8.3.2.0")])],"isStart":true})});
            var Q143;
            Q143=makeQuery(id+"F7.boolean.opBoolean","COPY",EDGE,{"derivedFrom":makeQuery(id+"F7.opExtrude","CAP_EDGE",EDGE,{"disambiguationData":[OSD([sQuery(id+"F6.wireOp",EDGE,"E8.3.1.0")])],"isStart":true})});
            var Q144;
            Q144=makeQuery(id+"F7.boolean.opBoolean","COPY",EDGE,{"derivedFrom":makeQuery(id+"F7.opExtrude","CAP_EDGE",EDGE,{"disambiguationData":[OSD([sQuery(id+"F6.wireOp",EDGE,"E8.3.0.0")])],"isStart":true})});
            var Q145;
            Q145=makeQuery(id+"F7.boolean.opBoolean","COPY",EDGE,{"derivedFrom":makeQuery(id+"F7.opExtrude","CAP_EDGE",EDGE,{"disambiguationData":[OSD([sQuery(id+"F6.wireOp",EDGE,"E8.2.14.0")])],"isStart":true})});
            var Q146;
            Q146=makeQuery(id+"F7.boolean.opBoolean","COPY",EDGE,{"derivedFrom":makeQuery(id+"F7.opExtrude","CAP_EDGE",EDGE,{"disambiguationData":[OSD([sQuery(id+"F6.wireOp",EDGE,"E8.2.13.0")])],"isStart":true})});
            var Q147;
            Q147=makeQuery(id+"F7.boolean.opBoolean","COPY",EDGE,{"derivedFrom":makeQuery(id+"F7.opExtrude","CAP_EDGE",EDGE,{"disambiguationData":[OSD([sQuery(id+"F6.wireOp",EDGE,"E8.2.12.0")])],"isStart":true})});
            var Q148;
            Q148=makeQuery(id+"F7.boolean.opBoolean","COPY",EDGE,{"derivedFrom":makeQuery(id+"F7.opExtrude","CAP_EDGE",EDGE,{"disambiguationData":[OSD([sQuery(id+"F6.wireOp",EDGE,"E8.2.11.0")])],"isStart":true})});
            var Q149;
            Q149=makeQuery(id+"F7.boolean.opBoolean","COPY",EDGE,{"derivedFrom":makeQuery(id+"F7.opExtrude","CAP_EDGE",EDGE,{"disambiguationData":[OSD([sQuery(id+"F6.wireOp",EDGE,"E8.2.10.0")])],"isStart":true})});
            var Q150;
            Q150=makeQuery(id+"F7.boolean.opBoolean","COPY",EDGE,{"derivedFrom":makeQuery(id+"F7.opExtrude","CAP_EDGE",EDGE,{"disambiguationData":[OSD([sQuery(id+"F6.wireOp",EDGE,"E8.2.9.0")])],"isStart":true})});
            var Q151;
            Q151=makeQuery(id+"F7.boolean.opBoolean","COPY",EDGE,{"derivedFrom":makeQuery(id+"F7.opExtrude","CAP_EDGE",EDGE,{"disambiguationData":[OSD([sQuery(id+"F6.wireOp",EDGE,"E8.2.8.0")])],"isStart":true})});
            var Q152;
            Q152=makeQuery(id+"F7.boolean.opBoolean","COPY",EDGE,{"derivedFrom":makeQuery(id+"F7.opExtrude","CAP_EDGE",EDGE,{"disambiguationData":[OSD([sQuery(id+"F6.wireOp",EDGE,"E8.2.7.0")])],"isStart":true})});
            var Q153;
            Q153=makeQuery(id+"F7.boolean.opBoolean","COPY",EDGE,{"derivedFrom":makeQuery(id+"F7.opExtrude","CAP_EDGE",EDGE,{"disambiguationData":[OSD([sQuery(id+"F6.wireOp",EDGE,"E8.2.6.0")])],"isStart":true})});
            var Q154;
            Q154=makeQuery(id+"F7.boolean.opBoolean","COPY",EDGE,{"derivedFrom":makeQuery(id+"F7.opExtrude","CAP_EDGE",EDGE,{"disambiguationData":[OSD([sQuery(id+"F6.wireOp",EDGE,"E8.2.5.0")])],"isStart":true})});
            var Q155;
            Q155=makeQuery(id+"F7.boolean.opBoolean","COPY",EDGE,{"derivedFrom":makeQuery(id+"F7.opExtrude","CAP_EDGE",EDGE,{"disambiguationData":[OSD([sQuery(id+"F6.wireOp",EDGE,"E8.2.4.0")])],"isStart":true})});
            var Q156;
            Q156=makeQuery(id+"F7.boolean.opBoolean","COPY",EDGE,{"derivedFrom":makeQuery(id+"F7.opExtrude","CAP_EDGE",EDGE,{"disambiguationData":[OSD([sQuery(id+"F6.wireOp",EDGE,"E8.2.3.0")])],"isStart":true})});
            var Q157;
            Q157=makeQuery(id+"F7.boolean.opBoolean","COPY",EDGE,{"derivedFrom":makeQuery(id+"F7.opExtrude","CAP_EDGE",EDGE,{"disambiguationData":[OSD([sQuery(id+"F6.wireOp",EDGE,"E8.2.2.0")])],"isStart":true})});
            var Q158;
            Q158=makeQuery(id+"F7.boolean.opBoolean","COPY",EDGE,{"derivedFrom":makeQuery(id+"F7.opExtrude","CAP_EDGE",EDGE,{"disambiguationData":[OSD([sQuery(id+"F6.wireOp",EDGE,"E8.2.1.0")])],"isStart":true})});
            var Q159;
            Q159=makeQuery(id+"F7.boolean.opBoolean","COPY",EDGE,{"derivedFrom":makeQuery(id+"F7.opExtrude","CAP_EDGE",EDGE,{"disambiguationData":[OSD([sQuery(id+"F6.wireOp",EDGE,"E8.2.0.0")])],"isStart":true})});
            var Q160;
            Q160=makeQuery(id+"F7.boolean.opBoolean","COPY",EDGE,{"derivedFrom":makeQuery(id+"F7.opExtrude","CAP_EDGE",EDGE,{"disambiguationData":[OSD([sQuery(id+"F6.wireOp",EDGE,"E8.1.14.0")])],"isStart":true})});
            var Q161;
            Q161=makeQuery(id+"F7.boolean.opBoolean","COPY",EDGE,{"derivedFrom":makeQuery(id+"F7.opExtrude","CAP_EDGE",EDGE,{"disambiguationData":[OSD([sQuery(id+"F6.wireOp",EDGE,"E8.1.13.0")])],"isStart":true})});
            var Q162;
            Q162=makeQuery(id+"F7.boolean.opBoolean","COPY",EDGE,{"derivedFrom":makeQuery(id+"F7.opExtrude","CAP_EDGE",EDGE,{"disambiguationData":[OSD([sQuery(id+"F6.wireOp",EDGE,"E8.1.12.0")])],"isStart":true})});
            var Q163;
            Q163=makeQuery(id+"F7.boolean.opBoolean","COPY",EDGE,{"derivedFrom":makeQuery(id+"F7.opExtrude","CAP_EDGE",EDGE,{"disambiguationData":[OSD([sQuery(id+"F6.wireOp",EDGE,"E8.1.11.0")])],"isStart":true})});
            var Q164;
            Q164=makeQuery(id+"F7.boolean.opBoolean","COPY",EDGE,{"derivedFrom":makeQuery(id+"F7.opExtrude","CAP_EDGE",EDGE,{"disambiguationData":[OSD([sQuery(id+"F6.wireOp",EDGE,"E8.1.10.0")])],"isStart":true})});
            var Q165;
            Q165=makeQuery(id+"F7.boolean.opBoolean","COPY",EDGE,{"derivedFrom":makeQuery(id+"F7.opExtrude","CAP_EDGE",EDGE,{"disambiguationData":[OSD([sQuery(id+"F6.wireOp",EDGE,"E8.1.9.0")])],"isStart":true})});
            var Q166;
            Q166=makeQuery(id+"F7.boolean.opBoolean","COPY",EDGE,{"derivedFrom":makeQuery(id+"F7.opExtrude","CAP_EDGE",EDGE,{"disambiguationData":[OSD([sQuery(id+"F6.wireOp",EDGE,"E8.1.8.0")])],"isStart":true})});
            var Q167;
            Q167=makeQuery(id+"F7.boolean.opBoolean","COPY",EDGE,{"derivedFrom":makeQuery(id+"F7.opExtrude","CAP_EDGE",EDGE,{"disambiguationData":[OSD([sQuery(id+"F6.wireOp",EDGE,"E8.1.7.0")])],"isStart":true})});
            var Q168;
            Q168=makeQuery(id+"F7.boolean.opBoolean","COPY",EDGE,{"derivedFrom":makeQuery(id+"F7.opExtrude","CAP_EDGE",EDGE,{"disambiguationData":[OSD([sQuery(id+"F6.wireOp",EDGE,"E8.1.6.0")])],"isStart":true})});
            var Q169;
            Q169=makeQuery(id+"F7.boolean.opBoolean","COPY",EDGE,{"derivedFrom":makeQuery(id+"F7.opExtrude","CAP_EDGE",EDGE,{"disambiguationData":[OSD([sQuery(id+"F6.wireOp",EDGE,"E8.1.5.0")])],"isStart":true})});
            var Q170;
            Q170=makeQuery(id+"F7.boolean.opBoolean","COPY",EDGE,{"derivedFrom":makeQuery(id+"F7.opExtrude","CAP_EDGE",EDGE,{"disambiguationData":[OSD([sQuery(id+"F6.wireOp",EDGE,"E8.1.4.0")])],"isStart":true})});
            var Q171;
            Q171=makeQuery(id+"F7.boolean.opBoolean","COPY",EDGE,{"derivedFrom":makeQuery(id+"F7.opExtrude","CAP_EDGE",EDGE,{"disambiguationData":[OSD([sQuery(id+"F6.wireOp",EDGE,"E8.1.3.0")])],"isStart":true})});
            var Q172;
            Q172=makeQuery(id+"F7.boolean.opBoolean","COPY",EDGE,{"derivedFrom":makeQuery(id+"F7.opExtrude","CAP_EDGE",EDGE,{"disambiguationData":[OSD([sQuery(id+"F6.wireOp",EDGE,"E8.1.2.0")])],"isStart":true})});
            var Q173;
            Q173=makeQuery(id+"F7.boolean.opBoolean","COPY",EDGE,{"derivedFrom":makeQuery(id+"F7.opExtrude","CAP_EDGE",EDGE,{"disambiguationData":[OSD([sQuery(id+"F6.wireOp",EDGE,"E8.1.1.0")])],"isStart":true})});
            var Q174;
            Q174=makeQuery(id+"F7.boolean.opBoolean","COPY",EDGE,{"derivedFrom":makeQuery(id+"F7.opExtrude","CAP_EDGE",EDGE,{"disambiguationData":[OSD([sQuery(id+"F6.wireOp",EDGE,"E8.1.0.0")])],"isStart":true})});
            var Q175;
            Q175=makeQuery(id+"F7.boolean.opBoolean","COPY",EDGE,{"derivedFrom":makeQuery(id+"F7.opExtrude","CAP_EDGE",EDGE,{"disambiguationData":[OSD([sQuery(id+"F6.wireOp",EDGE,"E9.0.8.19")])],"isStart":true})});
            var Q176;
            Q176=makeQuery(id+"F7.boolean.opBoolean","COPY",EDGE,{"derivedFrom":makeQuery(id+"F7.opExtrude","CAP_EDGE",EDGE,{"disambiguationData":[OSD([sQuery(id+"F6.wireOp",EDGE,"E9.0.8.18")])],"isStart":true})});
            var Q177;
            Q177=makeQuery(id+"F7.boolean.opBoolean","COPY",EDGE,{"derivedFrom":makeQuery(id+"F7.opExtrude","CAP_EDGE",EDGE,{"disambiguationData":[OSD([sQuery(id+"F6.wireOp",EDGE,"E9.0.8.17")])],"isStart":true})});
            var Q178;
            Q178=makeQuery(id+"F7.boolean.opBoolean","COPY",EDGE,{"derivedFrom":makeQuery(id+"F7.opExtrude","CAP_EDGE",EDGE,{"disambiguationData":[OSD([sQuery(id+"F6.wireOp",EDGE,"E9.0.8.16")])],"isStart":true})});
            var Q179;
            Q179=makeQuery(id+"F7.boolean.opBoolean","COPY",EDGE,{"derivedFrom":makeQuery(id+"F7.opExtrude","CAP_EDGE",EDGE,{"disambiguationData":[OSD([sQuery(id+"F6.wireOp",EDGE,"E9.0.8.15")])],"isStart":true})});
            var Q180;
            Q180=makeQuery(id+"F7.boolean.opBoolean","COPY",EDGE,{"derivedFrom":makeQuery(id+"F7.opExtrude","CAP_EDGE",EDGE,{"disambiguationData":[OSD([sQuery(id+"F6.wireOp",EDGE,"E9.0.8.18")])],"isStart":false})});
            var Q181;
            Q181=makeQuery(id+"F7.boolean.opBoolean","COPY",EDGE,{"derivedFrom":makeQuery(id+"F7.opExtrude","CAP_EDGE",EDGE,{"disambiguationData":[OSD([sQuery(id+"F6.wireOp",EDGE,"E9.0.8.17")])],"isStart":false})});
            var Q182;
            Q182=makeQuery(id+"F7.boolean.opBoolean","COPY",EDGE,{"derivedFrom":makeQuery(id+"F7.opExtrude","CAP_EDGE",EDGE,{"disambiguationData":[OSD([sQuery(id+"F6.wireOp",EDGE,"E9.0.8.19")])],"isStart":false})});
            var Q183;
            Q183=makeQuery(id+"F7.boolean.opBoolean","COPY",EDGE,{"derivedFrom":makeQuery(id+"F7.opExtrude","CAP_EDGE",EDGE,{"disambiguationData":[OSD([sQuery(id+"F6.wireOp",EDGE,"E9.0.8.15")])],"isStart":false})});
            var Q184;
            Q184=makeQuery(id+"F7.boolean.opBoolean","COPY",EDGE,{"derivedFrom":makeQuery(id+"F7.opExtrude","CAP_EDGE",EDGE,{"disambiguationData":[OSD([sQuery(id+"F6.wireOp",EDGE,"E9.0.8.16")])],"isStart":false})});
            chamfer(context, id + "F8", {"entities" : qUnion([Q0, Q1, Q2, Q3, Q4, Q5, Q6, Q7, Q8, Q9, Q10, Q11, Q12, Q13, Q14, Q15, Q16, Q17, Q18, Q19, Q20, Q21, Q22, Q23, Q24, Q25, Q26, Q27, Q28, Q29, Q30, Q31, Q32, Q33, Q34, Q35, Q36, Q37, Q38, Q39, Q40, Q41, Q42, Q43, Q44, Q45, Q46, Q47, Q48, Q49, Q50, Q51, Q52, Q53, Q54, Q55, Q56, Q57, Q58, Q59, Q60, Q61, Q62, Q63, Q64, Q65, Q66, Q67, Q68, Q69, Q70, Q71, Q72, Q73, Q74, Q75, Q76, Q77, Q78, Q79, Q80, Q81, Q82, Q83, Q84, Q85, Q86, Q87, Q88, Q89, Q90, Q91, Q92, Q93, Q94, Q95, Q96, Q97, Q98, Q99, Q100, Q101, Q102, Q103, Q104, Q105, Q106, Q107, Q108, Q109, Q110, Q111, Q112, Q113, Q114, Q115, Q116, Q117, Q118, Q119, Q120, Q121, Q122, Q123, Q124, Q125, Q126, Q127, Q128, Q129, Q130, Q131, Q132, Q133, Q134, Q135, Q136, Q137, Q138, Q139, Q140, Q141, Q142, Q143, Q144, Q145, Q146, Q147, Q148, Q149, Q150, Q151, Q152, Q153, Q154, Q155, Q156, Q157, Q158, Q159, Q160, Q161, Q162, Q163, Q164, Q165, Q166, Q167, Q168, Q169, Q170, Q171, Q172, Q173, Q174, Q175, Q176, Q177, Q178, Q179, Q180, Q181, Q182, Q183, Q184]), "width" : 0.5 * mm, "tangentPropagation" : true});
        }
        {
            var Q0;
            Q0=qCreatedBy(makeId("Front.planeOp"),FACE);
            var sketch = newSketch(context, id + "F9", { "sketchPlane" : qUnion([Q0])});
            skLineSegment(sketch, "E10", {"start": v(0, 0) * mm, "end": v(0, -190.27) * mm, "construction": true});
            skSolve(sketch);
        }
        {
            var Q0;
            Q0=makeQuery(id+"F0.imprint","IMPRINT",FACE,{"disambiguationData":[TD([[makeQuery(id+"F0.imprint","IMPRINT",EDGE,{"derivedFrom":sQuery(id+"F0.wireOp",EDGE,"E0.bottom")}),1.0]])]});
            var sketch = newSketch(context, id + "F10", { "sketchPlane" : qUnion([Q0])});
            skLineSegment(sketch, "E11.bottom", {"start": v(-177.8, 177.8) * mm, "end": v(177.8, 177.8) * mm});
            skLineSegment(sketch, "E11.top", {"start": v(-177.8, -177.8) * mm, "end": v(177.8, -177.8) * mm});
            skLineSegment(sketch, "E11.left", {"start": v(-177.8, 177.8) * mm, "end": v(-177.8, -177.8) * mm});
            skLineSegment(sketch, "E11.right", {"start": v(177.8, 177.8) * mm, "end": v(177.8, -177.8) * mm});
            skPoint(sketch, "E11.middle", {"position": v(0, 0) * mm});
            skSolve(sketch);
        }
        {
            var Q0;
            Q0=qSketchRegion(id+"F10",true);
            var Q1;
            Q1=makeQuery(id+"F10.imprint","IMPRINT",FACE,{"disambiguationData":[TD([[makeQuery(id+"F10.imprint","IMPRINT",EDGE,{"derivedFrom":sQuery(id+"F10.wireOp",EDGE,"E11.bottom")}),-1.0]])]});
            extrude(context, id + "F11", {"entities" : qUnion([Q0, Q1]), "oppositeDirection" : true, "depth" : 139.7 * mm, "hasSecondDirection" : true, "secondDirectionOppositeDirection" : true, "secondDirectionDepth" : 63.5 * mm});
        }
        {
            var Q0;
            Q0=makeQuery(id+"F11.opExtrude","CAP_FACE",FACE,{"disambiguationData":[OSD([sQuery(id+"F10.wireOp",EDGE,"E11.bottom"),sQuery(id+"F10.wireOp",EDGE,"E11.top"),sQuery(id+"F10.wireOp",EDGE,"E11.left"),sQuery(id+"F10.wireOp",EDGE,"E11.right")])],"isStart":true});
            var Q1;
            Q1=makeQuery(id+"F11.opExtrude","CAP_FACE",FACE,{"disambiguationData":[OSD([sQuery(id+"F10.wireOp",EDGE,"E11.bottom"),sQuery(id+"F10.wireOp",EDGE,"E11.top"),sQuery(id+"F10.wireOp",EDGE,"E11.left"),sQuery(id+"F10.wireOp",EDGE,"E11.right")])],"isStart":false});
            chamfer(context, id + "F12", {"entities" : qUnion([Q0, Q1]), "width" : 3.17 * mm, "tangentPropagation" : true});
        }
        {
            var Q0;
            Q0=makeQuery(id+"F11.opExtrude","SWEPT_FACE",FACE,{"disambiguationData":[OSD([sQuery(id+"F10.wireOp",EDGE,"E11.bottom")])]});
            var sketch = newSketch(context, id + "F13", { "sketchPlane" : qUnion([Q0])});
            skLineSegment(sketch, "E12.bottom", {"start": v(-158.75, -38.1) * mm, "end": v(-44.45, -38.1) * mm});
            skLineSegment(sketch, "E12.top", {"start": v(-158.75, -101.6) * mm, "end": v(-44.45, -101.6) * mm});
            skLineSegment(sketch, "E12.left", {"start": v(-158.75, -38.1) * mm, "end": v(-158.75, -101.6) * mm});
            skLineSegment(sketch, "E12.right", {"start": v(-44.45, -38.1) * mm, "end": v(-44.45, -101.6) * mm});
            skPoint(sketch, "E12.middle", {"position": v(-109.84, -66.67) * mm});
            skCircle(sketch, "E13", {"center": v(-139.7, -82.55) * mm, "radius": 9.53 * mm});
            skCircle(sketch, "E14", {"center": v(-63.5, -82.55) * mm, "radius": 9.53 * mm});
            skCircle(sketch, "E15", {"center": v(-139.7, -82.55) * mm, "radius": 6.35 * mm});
            skCircle(sketch, "E16", {"center": v(-63.5, -82.55) * mm, "radius": 6.35 * mm});
            skLineSegment(sketch, "E17.MirrorCS", {"start": v(158.75, -38.1) * mm, "end": v(44.45, -38.1) * mm});
            skLineSegment(sketch, "E18.MirrorCS", {"start": v(44.45, -38.1) * mm, "end": v(44.45, -101.6) * mm});
            skLineSegment(sketch, "E19.MirrorCS", {"start": v(158.75, -101.6) * mm, "end": v(44.45, -101.6) * mm});
            skLineSegment(sketch, "E20.MirrorCS", {"start": v(158.75, -38.1) * mm, "end": v(158.75, -101.6) * mm});
            skCircle(sketch, "E21.MirrorC", {"center": v(139.7, -82.55) * mm, "radius": 9.53 * mm});
            skCircle(sketch, "E22.MirrorC", {"center": v(139.7, -82.55) * mm, "radius": 6.35 * mm});
            skCircle(sketch, "E23.MirrorC", {"center": v(63.5, -82.55) * mm, "radius": 9.53 * mm});
            skCircle(sketch, "E24.MirrorC", {"center": v(63.5, -82.55) * mm, "radius": 6.35 * mm});
            skSolve(sketch);
        }
        {
            var Q0;
            {var subQ1=sQuery(id+"F13.wireOp",EDGE,"E12.top");Q0=makeQuery(id+"F13.imprint","IMPRINT",FACE,{"disambiguationData":[TD([[makeQuery(id+"F13.imprint","IMPRINT",EDGE,{"derivedFrom":subQ1}),1.0]])]});}
            var Q1;
            {var subQ0=sQuery(id+"F13.wireOp",EDGE,"E12.bottom");Q1=makeQuery(id+"F13.imprint","IMPRINT",FACE,{"disambiguationData":[TD([[makeQuery(id+"F13.imprint","IMPRINT",EDGE,{"derivedFrom":subQ0}),-1.0]])]});}
            var Q2;
            {var subQ0=sQuery(id+"F13.wireOp",EDGE,"E17.MirrorCS");Q2=makeQuery(id+"F13.imprint","IMPRINT",FACE,{"disambiguationData":[TD([[makeQuery(id+"F13.imprint","IMPRINT",EDGE,{"derivedFrom":subQ0}),1.0]])]});}
            var Q3;
            {var subQ6=sQuery(id+"F13.wireOp",EDGE,"E19.MirrorCS");Q3=makeQuery(id+"F13.imprint","IMPRINT",FACE,{"disambiguationData":[TD([[makeQuery(id+"F13.imprint","IMPRINT",EDGE,{"derivedFrom":subQ6}),-1.0]])]});}
            var Q4;
            Q4=makeQuery(id+"F13.imprint","IMPRINT",FACE,{"disambiguationData":[TD([[makeQuery(id+"F13.imprint","IMPRINT",EDGE,{"derivedFrom":sQuery(id+"F13.wireOp",EDGE,"E23.MirrorC")}),-1.0]])]});
            var Q5;
            Q5=makeQuery(id+"F13.imprint","IMPRINT",FACE,{"disambiguationData":[TD([[makeQuery(id+"F13.imprint","IMPRINT",EDGE,{"derivedFrom":sQuery(id+"F13.wireOp",EDGE,"E14")}),1.0]])]});
            var Q6;
            Q6=makeQuery(id+"F13.imprint","IMPRINT",FACE,{"disambiguationData":[TD([[makeQuery(id+"F13.imprint","IMPRINT",EDGE,{"derivedFrom":sQuery(id+"F13.wireOp",EDGE,"E13")}),1.0]])]});
            var Q7;
            Q7=makeQuery(id+"F13.imprint","IMPRINT",FACE,{"disambiguationData":[TD([[makeQuery(id+"F13.imprint","IMPRINT",EDGE,{"derivedFrom":sQuery(id+"F13.wireOp",EDGE,"E21.MirrorC")}),-1.0]])]});
            extrude(context, id + "F14", {"entities" : qUnion([Q0, Q1, Q2, Q3, Q4, Q5, Q6, Q7]), "depth" : 15.88 * mm});
        }
        {
            var Q0;
            Q0=makeQuery(id+"F13.imprint","IMPRINT",FACE,{"disambiguationData":[TD([[makeQuery(id+"F13.imprint","IMPRINT",EDGE,{"derivedFrom":sQuery(id+"F13.wireOp",EDGE,"E13")}),1.0]])]});
            var Q1;
            Q1=makeQuery(id+"F13.imprint","IMPRINT",FACE,{"disambiguationData":[TD([[makeQuery(id+"F13.imprint","IMPRINT",EDGE,{"derivedFrom":sQuery(id+"F13.wireOp",EDGE,"E14")}),1.0]])]});
            var Q2;
            Q2=makeQuery(id+"F13.imprint","IMPRINT",FACE,{"disambiguationData":[TD([[makeQuery(id+"F13.imprint","IMPRINT",EDGE,{"derivedFrom":sQuery(id+"F13.wireOp",EDGE,"E23.MirrorC")}),-1.0]])]});
            var Q3;
            Q3=makeQuery(id+"F13.imprint","IMPRINT",FACE,{"disambiguationData":[TD([[makeQuery(id+"F13.imprint","IMPRINT",EDGE,{"derivedFrom":sQuery(id+"F13.wireOp",EDGE,"E21.MirrorC")}),-1.0]])]});
            extrude(context, id + "F15", {"entities" : qUnion([Q0, Q1, Q2, Q3]), "operationType" : NewBodyOperationType.REMOVE, "depth" : 25.4 * mm, "hasSecondDirection" : true, "secondDirectionOppositeDirection" : false, "secondDirectionDepth" : 3.17 * mm, "offsetDistance" : 25.4 * mm});
        }
        {
            var Q0;
            Q0=makeQuery(id+"F14.opExtrude","SWEPT_BODY",BODY,{"disambiguationData":[OSD([sQuery(id+"F13.wireOp",EDGE,"E12.bottom"),sQuery(id+"F13.wireOp",EDGE,"E12.top"),sQuery(id+"F13.wireOp",EDGE,"E12.left"),sQuery(id+"F13.wireOp",EDGE,"E12.right"),sQuery(id+"F13.wireOp",EDGE,"E15"),sQuery(id+"F13.wireOp",EDGE,"E16")])]});
            var Q1;
            Q1=makeQuery(id+"F14.opExtrude","SWEPT_BODY",BODY,{"disambiguationData":[OSD([sQuery(id+"F13.wireOp",EDGE,"E17.MirrorCS"),sQuery(id+"F13.wireOp",EDGE,"E18.MirrorCS"),sQuery(id+"F13.wireOp",EDGE,"E19.MirrorCS"),sQuery(id+"F13.wireOp",EDGE,"E20.MirrorCS"),sQuery(id+"F13.wireOp",EDGE,"E22.MirrorC"),sQuery(id+"F13.wireOp",EDGE,"E24.MirrorC")])]});
            var Q2;
            Q2=sQuery(id+"F9.wireOp",EDGE,"E10");
            circularPattern(context, id + "F16", {"entities" : qUnion([Q0, Q1]), "axis" : qUnion([Q2]), "angle" : 90 * degree, "instanceCount" : 2, "equalSpace" : true});
        }
        {
            var Q0;
            Q0=makeQuery(id+"F14.opExtrude","CAP_FACE",FACE,{"disambiguationData":[OSD([sQuery(id+"F13.wireOp",EDGE,"E12.bottom"),sQuery(id+"F13.wireOp",EDGE,"E12.top"),sQuery(id+"F13.wireOp",EDGE,"E12.left"),sQuery(id+"F13.wireOp",EDGE,"E12.right"),sQuery(id+"F13.wireOp",EDGE,"E15"),sQuery(id+"F13.wireOp",EDGE,"E16")])],"isStart":false});
            var Q1;
            Q1=makeQuery(id+"F14.opExtrude","CAP_FACE",FACE,{"disambiguationData":[OSD([sQuery(id+"F13.wireOp",EDGE,"E17.MirrorCS"),sQuery(id+"F13.wireOp",EDGE,"E18.MirrorCS"),sQuery(id+"F13.wireOp",EDGE,"E19.MirrorCS"),sQuery(id+"F13.wireOp",EDGE,"E20.MirrorCS"),sQuery(id+"F13.wireOp",EDGE,"E22.MirrorC"),sQuery(id+"F13.wireOp",EDGE,"E24.MirrorC")])],"isStart":false});
            var Q2;
            Q2=makeQuery(id+"F16.opPattern","COPY",FACE,{"derivedFrom":makeQuery(id+"F14.opExtrude","CAP_FACE",FACE,{"disambiguationData":[OSD([sQuery(id+"F13.wireOp",EDGE,"E17.MirrorCS"),sQuery(id+"F13.wireOp",EDGE,"E18.MirrorCS"),sQuery(id+"F13.wireOp",EDGE,"E19.MirrorCS"),sQuery(id+"F13.wireOp",EDGE,"E20.MirrorCS"),sQuery(id+"F13.wireOp",EDGE,"E22.MirrorC"),sQuery(id+"F13.wireOp",EDGE,"E24.MirrorC")])],"isStart":false}),"instanceName":"1"});
            var Q3;
            Q3=makeQuery(id+"F16.opPattern","COPY",FACE,{"derivedFrom":makeQuery(id+"F14.opExtrude","CAP_FACE",FACE,{"disambiguationData":[OSD([sQuery(id+"F13.wireOp",EDGE,"E12.bottom"),sQuery(id+"F13.wireOp",EDGE,"E12.top"),sQuery(id+"F13.wireOp",EDGE,"E12.left"),sQuery(id+"F13.wireOp",EDGE,"E12.right"),sQuery(id+"F13.wireOp",EDGE,"E15"),sQuery(id+"F13.wireOp",EDGE,"E16")])],"isStart":false}),"instanceName":"1"});
            var Q4;
            Q4=makeQuery(id+"F16.opPattern","COPY",EDGE,{"derivedFrom":makeQuery(id+"F14.opExtrude","SWEPT_EDGE",EDGE,{"disambiguationData":[OSD([sQuery(id+"F13.wireOp",EDGE,"E17.MirrorCS"),sQuery(id+"F13.wireOp",EDGE,"E20.MirrorCS")])]}),"instanceName":"1"});
            var Q5;
            Q5=makeQuery(id+"F16.opPattern","COPY",EDGE,{"derivedFrom":makeQuery(id+"F14.opExtrude","SWEPT_EDGE",EDGE,{"disambiguationData":[OSD([sQuery(id+"F13.wireOp",EDGE,"E17.MirrorCS"),sQuery(id+"F13.wireOp",EDGE,"E18.MirrorCS")])]}),"instanceName":"1"});
            var Q6;
            Q6=makeQuery(id+"F16.opPattern","COPY",EDGE,{"derivedFrom":makeQuery(id+"F14.opExtrude","SWEPT_EDGE",EDGE,{"disambiguationData":[OSD([sQuery(id+"F13.wireOp",EDGE,"E12.bottom"),sQuery(id+"F13.wireOp",EDGE,"E12.right")])]}),"instanceName":"1"});
            var Q7;
            Q7=makeQuery(id+"F16.opPattern","COPY",EDGE,{"derivedFrom":makeQuery(id+"F14.opExtrude","SWEPT_EDGE",EDGE,{"disambiguationData":[OSD([sQuery(id+"F13.wireOp",EDGE,"E12.bottom"),sQuery(id+"F13.wireOp",EDGE,"E12.left")])]}),"instanceName":"1"});
            var Q8;
            Q8=makeQuery(id+"F14.opExtrude","SWEPT_EDGE",EDGE,{"disambiguationData":[OSD([sQuery(id+"F13.wireOp",EDGE,"E12.bottom"),sQuery(id+"F13.wireOp",EDGE,"E12.left")])]});
            var Q9;
            Q9=makeQuery(id+"F14.opExtrude","SWEPT_EDGE",EDGE,{"disambiguationData":[OSD([sQuery(id+"F13.wireOp",EDGE,"E17.MirrorCS"),sQuery(id+"F13.wireOp",EDGE,"E18.MirrorCS")])]});
            var Q10;
            Q10=makeQuery(id+"F14.opExtrude","SWEPT_EDGE",EDGE,{"disambiguationData":[OSD([sQuery(id+"F13.wireOp",EDGE,"E17.MirrorCS"),sQuery(id+"F13.wireOp",EDGE,"E20.MirrorCS")])]});
            var Q11;
            Q11=makeQuery(id+"F14.opExtrude","SWEPT_EDGE",EDGE,{"disambiguationData":[OSD([sQuery(id+"F13.wireOp",EDGE,"E18.MirrorCS"),sQuery(id+"F13.wireOp",EDGE,"E19.MirrorCS")])]});
            var Q12;
            Q12=makeQuery(id+"F14.opExtrude","SWEPT_EDGE",EDGE,{"disambiguationData":[OSD([sQuery(id+"F13.wireOp",EDGE,"E19.MirrorCS"),sQuery(id+"F13.wireOp",EDGE,"E20.MirrorCS")])]});
            var Q13;
            Q13=makeQuery(id+"F14.opExtrude","SWEPT_EDGE",EDGE,{"disambiguationData":[OSD([sQuery(id+"F13.wireOp",EDGE,"E12.top"),sQuery(id+"F13.wireOp",EDGE,"E12.left")])]});
            var Q14;
            Q14=makeQuery(id+"F16.opPattern","COPY",EDGE,{"derivedFrom":makeQuery(id+"F14.opExtrude","SWEPT_EDGE",EDGE,{"disambiguationData":[OSD([sQuery(id+"F13.wireOp",EDGE,"E19.MirrorCS"),sQuery(id+"F13.wireOp",EDGE,"E20.MirrorCS")])]}),"instanceName":"1"});
            var Q15;
            Q15=makeQuery(id+"F16.opPattern","COPY",EDGE,{"derivedFrom":makeQuery(id+"F14.opExtrude","SWEPT_EDGE",EDGE,{"disambiguationData":[OSD([sQuery(id+"F13.wireOp",EDGE,"E18.MirrorCS"),sQuery(id+"F13.wireOp",EDGE,"E19.MirrorCS")])]}),"instanceName":"1"});
            var Q16;
            Q16=makeQuery(id+"F16.opPattern","COPY",EDGE,{"derivedFrom":makeQuery(id+"F14.opExtrude","SWEPT_EDGE",EDGE,{"disambiguationData":[OSD([sQuery(id+"F13.wireOp",EDGE,"E12.top"),sQuery(id+"F13.wireOp",EDGE,"E12.left")])]}),"instanceName":"1"});
            var Q17;
            Q17=makeQuery(id+"F16.opPattern","COPY",EDGE,{"derivedFrom":makeQuery(id+"F14.opExtrude","SWEPT_EDGE",EDGE,{"disambiguationData":[OSD([sQuery(id+"F13.wireOp",EDGE,"E12.top"),sQuery(id+"F13.wireOp",EDGE,"E12.right")])]}),"instanceName":"1"});
            var Q18;
            Q18=makeQuery(id+"F16.opPattern","COPY",EDGE,{"derivedFrom":makeQuery(id+"F14.opExtrude","CAP_EDGE",EDGE,{"disambiguationData":[OSD([sQuery(id+"F13.wireOp",EDGE,"E12.top")])],"isStart":true}),"instanceName":"1"});
            var Q19;
            Q19=makeQuery(id+"F16.opPattern","COPY",EDGE,{"derivedFrom":makeQuery(id+"F14.opExtrude","CAP_EDGE",EDGE,{"disambiguationData":[OSD([sQuery(id+"F13.wireOp",EDGE,"E12.left")])],"isStart":true}),"instanceName":"1"});
            var Q20;
            Q20=makeQuery(id+"F16.opPattern","COPY",EDGE,{"derivedFrom":makeQuery(id+"F14.opExtrude","CAP_EDGE",EDGE,{"disambiguationData":[OSD([sQuery(id+"F13.wireOp",EDGE,"E12.right")])],"isStart":true}),"instanceName":"1"});
            var Q21;
            Q21=makeQuery(id+"F16.opPattern","COPY",EDGE,{"derivedFrom":makeQuery(id+"F14.opExtrude","CAP_EDGE",EDGE,{"disambiguationData":[OSD([sQuery(id+"F13.wireOp",EDGE,"E12.bottom")])],"isStart":true}),"instanceName":"1"});
            var Q22;
            Q22=makeQuery(id+"F16.opPattern","COPY",EDGE,{"derivedFrom":makeQuery(id+"F14.opExtrude","CAP_EDGE",EDGE,{"disambiguationData":[OSD([sQuery(id+"F13.wireOp",EDGE,"E17.MirrorCS")])],"isStart":true}),"instanceName":"1"});
            var Q23;
            Q23=makeQuery(id+"F14.opExtrude","CAP_EDGE",EDGE,{"disambiguationData":[OSD([sQuery(id+"F13.wireOp",EDGE,"E12.bottom")])],"isStart":true});
            var Q24;
            Q24=makeQuery(id+"F14.opExtrude","CAP_EDGE",EDGE,{"disambiguationData":[OSD([sQuery(id+"F13.wireOp",EDGE,"E17.MirrorCS")])],"isStart":true});
            var Q25;
            Q25=makeQuery(id+"F14.opExtrude","CAP_EDGE",EDGE,{"disambiguationData":[OSD([sQuery(id+"F13.wireOp",EDGE,"E18.MirrorCS")])],"isStart":true});
            var Q26;
            Q26=makeQuery(id+"F14.opExtrude","CAP_EDGE",EDGE,{"disambiguationData":[OSD([sQuery(id+"F13.wireOp",EDGE,"E12.left")])],"isStart":true});
            var Q27;
            Q27=makeQuery(id+"F14.opExtrude","CAP_EDGE",EDGE,{"disambiguationData":[OSD([sQuery(id+"F13.wireOp",EDGE,"E12.right")])],"isStart":true});
            var Q28;
            Q28=makeQuery(id+"F14.opExtrude","CAP_EDGE",EDGE,{"disambiguationData":[OSD([sQuery(id+"F13.wireOp",EDGE,"E20.MirrorCS")])],"isStart":true});
            var Q29;
            Q29=makeQuery(id+"F14.opExtrude","CAP_EDGE",EDGE,{"disambiguationData":[OSD([sQuery(id+"F13.wireOp",EDGE,"E19.MirrorCS")])],"isStart":true});
            var Q30;
            Q30=makeQuery(id+"F14.opExtrude","CAP_EDGE",EDGE,{"disambiguationData":[OSD([sQuery(id+"F13.wireOp",EDGE,"E12.top")])],"isStart":true});
            var Q31;
            Q31=makeQuery(id+"F16.opPattern","COPY",EDGE,{"derivedFrom":makeQuery(id+"F14.opExtrude","CAP_EDGE",EDGE,{"disambiguationData":[OSD([sQuery(id+"F13.wireOp",EDGE,"E19.MirrorCS")])],"isStart":true}),"instanceName":"1"});
            var Q32;
            Q32=makeQuery(id+"F16.opPattern","COPY",EDGE,{"derivedFrom":makeQuery(id+"F14.opExtrude","CAP_EDGE",EDGE,{"disambiguationData":[OSD([sQuery(id+"F13.wireOp",EDGE,"E18.MirrorCS")])],"isStart":true}),"instanceName":"1"});
            var Q33;
            Q33=makeQuery(id+"F16.opPattern","COPY",EDGE,{"derivedFrom":makeQuery(id+"F14.opExtrude","CAP_EDGE",EDGE,{"disambiguationData":[OSD([sQuery(id+"F13.wireOp",EDGE,"E20.MirrorCS")])],"isStart":true}),"instanceName":"1"});
            chamfer(context, id + "F17", {"entities" : qUnion([Q0, Q1, Q2, Q3, Q4, Q5, Q6, Q7, Q8, Q9, Q10, Q11, Q12, Q13, Q14, Q15, Q16, Q17, Q18, Q19, Q20, Q21, Q22, Q23, Q24, Q25, Q26, Q27, Q28, Q29, Q30, Q31, Q32, Q33]), "width" : 1.27 * mm, "tangentPropagation" : true});
        }
        {
            var Q0;
            Q0=makeQuery(id+"F1.opExtrude","SWEPT_FACE",FACE,{"disambiguationData":[OSD([sQuery(id+"F0.wireOp",EDGE,"E0.right")])]});
            var sketch = newSketch(context, id + "F18", { "sketchPlane" : qUnion([Q0])});
            skLineSegment(sketch, "E25", {"start": v(-99.3, 37.72) * mm, "end": v(103.9, 37.72) * mm});
            skText(sketch, "E26", { "text": "SIDE A   G54", "fontName": "NotoSerif-Bold.ttf"});
            const initialGuessF18  = {"E26": [-0.0993, 0.02534, 1, 0, 0.02386]};
            skSetInitialGuess(sketch, initialGuessF18);
            skSolve(sketch);
        }
        {
            var Q0;
            Q0=qSketchRegion(id+"F18",true);
            extrude(context, id + "F19", {"entities" : qUnion([Q0]), "operationType" : NewBodyOperationType.ADD, "depth" : 0.76 * mm, "offsetDistance" : 25.4 * mm});
        }
    });
